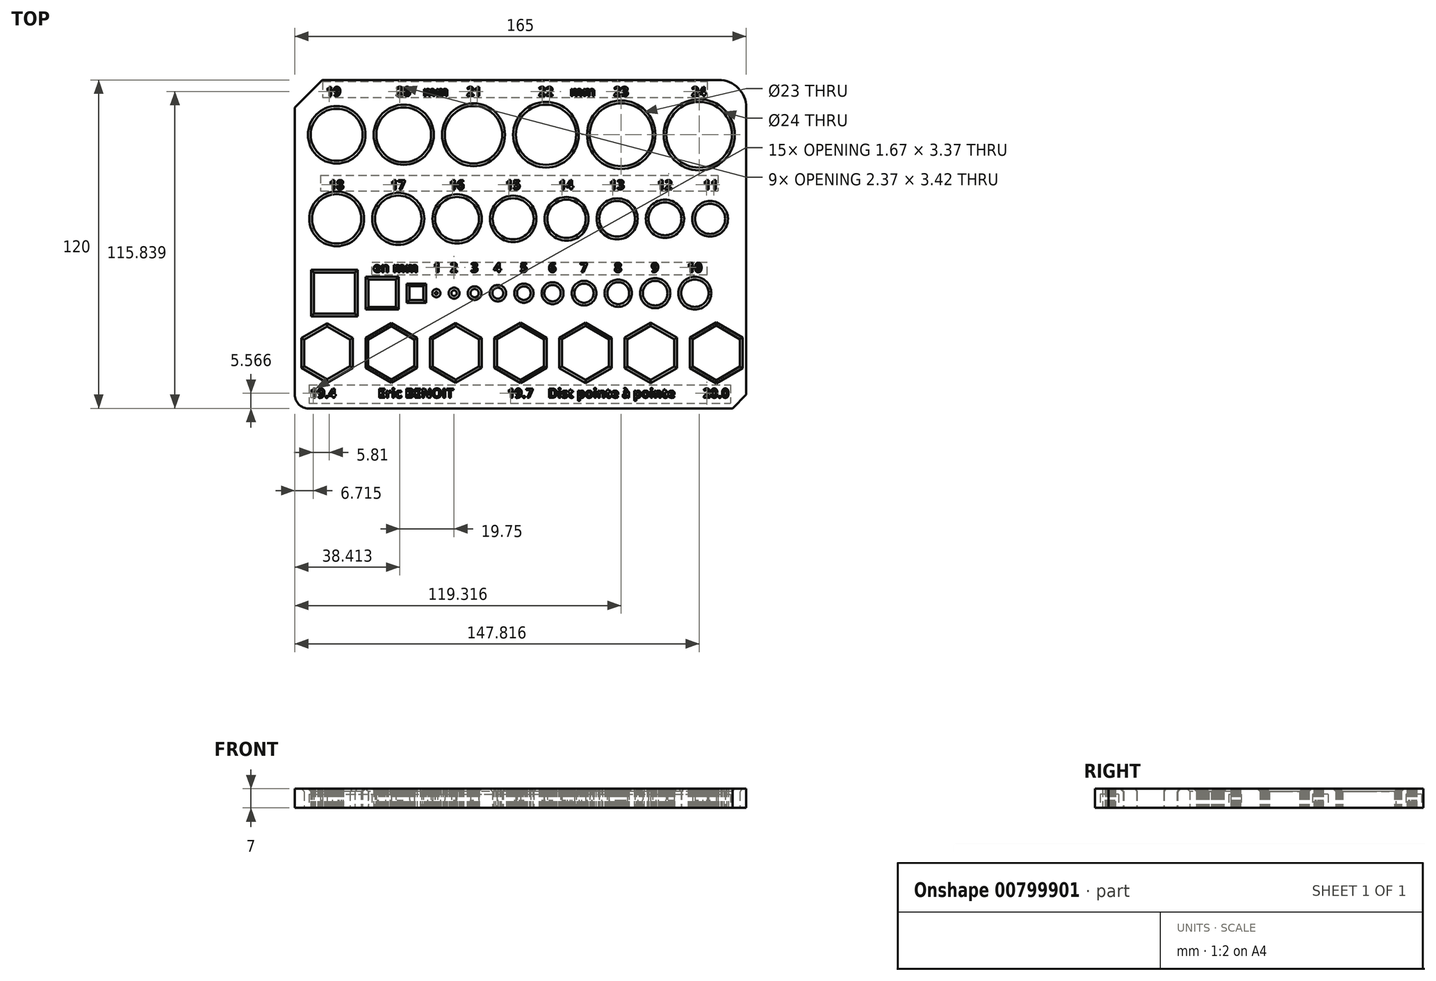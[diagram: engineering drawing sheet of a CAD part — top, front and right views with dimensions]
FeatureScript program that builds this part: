
annotation { "Feature Type Name" : "Feature", "Feature Type Description" : "" }
export const myFeature = defineFeature(function(context is Context, id is Id, definition is map)
    precondition{}
    {
        {
            var Q0;
            Q0=qCreatedBy(makeId("Top.planeOp"),FACE);
            var sketch = newSketch(context, id + "F0", { "sketchPlane" : qUnion([Q0])});
            skLineSegment(sketch, "E0.bottom", {"start": v(-82.5, 60) * mm, "end": v(82.5, 60) * mm});
            skLineSegment(sketch, "E0.top", {"start": v(-82.5, -60) * mm, "end": v(82.5, -60) * mm});
            skLineSegment(sketch, "E0.left", {"start": v(-82.5, 60) * mm, "end": v(-82.5, -60) * mm});
            skLineSegment(sketch, "E0.right", {"start": v(82.5, 60) * mm, "end": v(82.5, -60) * mm});
            skPoint(sketch, "E0.middle", {"position": v(0, 0) * mm});
            skLineSegment(sketch, "E1", {"start": v(-109.64, 40) * mm, "end": v(128.27, 40) * mm, "construction": true});
            skCircle(sketch, "E2", {"center": v(-67.18, 40) * mm, "radius": 9.5 * mm});
            skLineSegment(sketch, "E3.bottom", {"start": v(-57.68, 40) * mm, "end": v(-52.68, 40) * mm, "construction": true});
            skLineSegment(sketch, "E3.top", {"start": v(-57.68, 27.28) * mm, "end": v(-52.68, 27.28) * mm, "construction": true});
            skLineSegment(sketch, "E3.left", {"start": v(-57.68, 40) * mm, "end": v(-57.68, 27.28) * mm, "construction": true});
            skLineSegment(sketch, "E3.right", {"start": v(-52.68, 40) * mm, "end": v(-52.68, 27.28) * mm, "construction": true});
            skCircle(sketch, "E4", {"center": v(-42.68, 40) * mm, "radius": 10 * mm});
            skLineSegment(sketch, "E5.bottom", {"start": v(-32.68, 40) * mm, "end": v(-27.68, 40) * mm, "construction": true});
            skLineSegment(sketch, "E5.top", {"start": v(-32.68, 27.23) * mm, "end": v(-27.68, 27.23) * mm, "construction": true});
            skLineSegment(sketch, "E5.left", {"start": v(-32.68, 40) * mm, "end": v(-32.68, 27.23) * mm, "construction": true});
            skLineSegment(sketch, "E5.right", {"start": v(-27.68, 40) * mm, "end": v(-27.68, 27.23) * mm, "construction": true});
            skCircle(sketch, "E6", {"center": v(-17.18, 40) * mm, "radius": 10.5 * mm});
            skLineSegment(sketch, "E7.bottom", {"start": v(-6.68, 40) * mm, "end": v(-1.68, 40) * mm});
            skLineSegment(sketch, "E7.top", {"start": v(-6.68, 26.79) * mm, "end": v(-1.68, 26.79) * mm, "construction": true});
            skLineSegment(sketch, "E7.left", {"start": v(-6.68, 40) * mm, "end": v(-6.68, 26.79) * mm, "construction": true});
            skLineSegment(sketch, "E7.right", {"start": v(-1.68, 40) * mm, "end": v(-1.68, 26.79) * mm, "construction": true});
            skCircle(sketch, "E8", {"center": v(9.32, 40) * mm, "radius": 11 * mm});
            skLineSegment(sketch, "E9.bottom", {"start": v(20.32, 40) * mm, "end": v(25.32, 40) * mm});
            skLineSegment(sketch, "E9.top", {"start": v(20.32, 26.79) * mm, "end": v(25.32, 26.79) * mm, "construction": true});
            skLineSegment(sketch, "E9.left", {"start": v(20.32, 40) * mm, "end": v(20.32, 26.79) * mm, "construction": true});
            skLineSegment(sketch, "E9.right", {"start": v(25.32, 40) * mm, "end": v(25.32, 26.79) * mm, "construction": true});
            skCircle(sketch, "E10", {"center": v(36.82, 40) * mm, "radius": 11.5 * mm});
            skLineSegment(sketch, "E11.bottom", {"start": v(48.32, 40) * mm, "end": v(53.32, 40) * mm});
            skLineSegment(sketch, "E11.top", {"start": v(48.32, 25.73) * mm, "end": v(53.32, 25.73) * mm, "construction": true});
            skLineSegment(sketch, "E11.left", {"start": v(48.32, 40) * mm, "end": v(48.32, 25.73) * mm, "construction": true});
            skLineSegment(sketch, "E11.right", {"start": v(53.32, 40) * mm, "end": v(53.32, 25.73) * mm, "construction": true});
            skCircle(sketch, "E12", {"center": v(65.32, 40) * mm, "radius": 12 * mm});
            skLineSegment(sketch, "E13", {"start": v(-86.72, 9.27) * mm, "end": v(82.69, 9.27) * mm, "construction": true});
            skCircle(sketch, "E14", {"center": v(-67.18, 9.27) * mm, "radius": 9 * mm});
            skLineSegment(sketch, "E15.bottom", {"start": v(-58.18, 9.27) * mm, "end": v(-53.18, 9.27) * mm, "construction": true});
            skLineSegment(sketch, "E15.top", {"start": v(-58.18, -2.69) * mm, "end": v(-53.18, -2.69) * mm, "construction": true});
            skLineSegment(sketch, "E15.left", {"start": v(-58.18, 9.27) * mm, "end": v(-58.18, -2.69) * mm, "construction": true});
            skLineSegment(sketch, "E15.right", {"start": v(-53.18, 9.27) * mm, "end": v(-53.18, -2.69) * mm, "construction": true});
            skCircle(sketch, "E16", {"center": v(-44.68, 9.27) * mm, "radius": 8.5 * mm});
            skLineSegment(sketch, "E17.bottom", {"start": v(-36.18, 9.27) * mm, "end": v(-31.18, 9.27) * mm, "construction": true});
            skLineSegment(sketch, "E17.top", {"start": v(-36.18, -2.69) * mm, "end": v(-31.18, -2.69) * mm, "construction": true});
            skLineSegment(sketch, "E17.left", {"start": v(-36.18, 9.27) * mm, "end": v(-36.18, -2.69) * mm, "construction": true});
            skLineSegment(sketch, "E17.right", {"start": v(-31.18, 9.27) * mm, "end": v(-31.18, -2.69) * mm, "construction": true});
            skCircle(sketch, "E18", {"center": v(-23.18, 9.27) * mm, "radius": 8 * mm});
            skLineSegment(sketch, "E19.bottom", {"start": v(-15.18, 9.27) * mm, "end": v(-10.18, 9.27) * mm, "construction": true});
            skLineSegment(sketch, "E19.top", {"start": v(-15.18, -3.01) * mm, "end": v(-10.18, -3.01) * mm, "construction": true});
            skLineSegment(sketch, "E19.left", {"start": v(-15.18, 9.27) * mm, "end": v(-15.18, -3.01) * mm, "construction": true});
            skLineSegment(sketch, "E19.right", {"start": v(-10.18, 9.27) * mm, "end": v(-10.18, -3.01) * mm, "construction": true});
            skCircle(sketch, "E20", {"center": v(-2.68, 9.27) * mm, "radius": 7.5 * mm});
            skLineSegment(sketch, "E21.bottom", {"start": v(4.82, 9.27) * mm, "end": v(9.82, 9.27) * mm, "construction": true});
            skLineSegment(sketch, "E21.top", {"start": v(4.82, -2.69) * mm, "end": v(9.82, -2.69) * mm, "construction": true});
            skLineSegment(sketch, "E21.left", {"start": v(4.82, 9.27) * mm, "end": v(4.82, -2.69) * mm, "construction": true});
            skLineSegment(sketch, "E21.right", {"start": v(9.82, 9.27) * mm, "end": v(9.82, -2.69) * mm, "construction": true});
            skCircle(sketch, "E22", {"center": v(16.82, 9.27) * mm, "radius": 7 * mm});
            skLineSegment(sketch, "E23.bottom", {"start": v(23.82, 9.27) * mm, "end": v(28.82, 9.27) * mm, "construction": true});
            skLineSegment(sketch, "E23.top", {"start": v(23.82, -2.69) * mm, "end": v(28.82, -2.69) * mm, "construction": true});
            skLineSegment(sketch, "E23.left", {"start": v(23.82, 9.27) * mm, "end": v(23.82, -2.69) * mm, "construction": true});
            skLineSegment(sketch, "E23.right", {"start": v(28.82, 9.27) * mm, "end": v(28.82, -2.69) * mm, "construction": true});
            skCircle(sketch, "E24", {"center": v(35.32, 9.27) * mm, "radius": 6.5 * mm});
            skLineSegment(sketch, "E25.bottom", {"start": v(41.82, 9.27) * mm, "end": v(46.82, 9.27) * mm, "construction": true});
            skLineSegment(sketch, "E25.top", {"start": v(41.82, -2.69) * mm, "end": v(46.82, -2.69) * mm, "construction": true});
            skLineSegment(sketch, "E25.left", {"start": v(41.82, 9.27) * mm, "end": v(41.82, -2.69) * mm, "construction": true});
            skLineSegment(sketch, "E25.right", {"start": v(46.82, 9.27) * mm, "end": v(46.82, -2.69) * mm, "construction": true});
            skCircle(sketch, "E26", {"center": v(52.82, 9.27) * mm, "radius": 6 * mm});
            skLineSegment(sketch, "E27.bottom", {"start": v(58.82, 9.27) * mm, "end": v(63.82, 9.27) * mm, "construction": true});
            skLineSegment(sketch, "E27.top", {"start": v(58.82, -2.69) * mm, "end": v(63.82, -2.69) * mm, "construction": true});
            skLineSegment(sketch, "E27.left", {"start": v(58.82, 9.27) * mm, "end": v(58.82, -2.69) * mm, "construction": true});
            skLineSegment(sketch, "E27.right", {"start": v(63.82, 9.27) * mm, "end": v(63.82, -2.69) * mm, "construction": true});
            skCircle(sketch, "E28", {"center": v(69.32, 9.27) * mm, "radius": 5.5 * mm});
            skLineSegment(sketch, "E29", {"start": v(-83.6, 57.53) * mm, "end": v(84.67, 57.53) * mm, "construction": true});
            skLineSegment(sketch, "E30", {"start": v(-83.6, 54.13) * mm, "end": v(84.67, 54.13) * mm, "construction": true});
            skText(sketch, "E31", { "text": "19", "fontName": "OpenSans-Bold.ttf"});
            skText(sketch, "E32", { "text": "20", "fontName": "OpenSans-Bold.ttf"});
            skText(sketch, "E33", { "text": "21", "fontName": "OpenSans-Bold.ttf"});
            skText(sketch, "E34", { "text": "22", "fontName": "OpenSans-Bold.ttf"});
            skText(sketch, "E35", { "text": "23", "fontName": "OpenSans-Bold.ttf"});
            skText(sketch, "E36", { "text": "24", "fontName": "OpenSans-Bold.ttf"});
            skLineSegment(sketch, "E37", {"start": v(-86.72, 23.43) * mm, "end": v(82.69, 23.43) * mm, "construction": true});
            skLineSegment(sketch, "E38", {"start": v(-86.72, 20.03) * mm, "end": v(82.69, 20.03) * mm, "construction": true});
            skText(sketch, "E39", { "text": "18", "fontName": "OpenSans-Bold.ttf"});
            skText(sketch, "E40", { "text": "17", "fontName": "OpenSans-Bold.ttf"});
            skText(sketch, "E41", { "text": "16", "fontName": "OpenSans-Bold.ttf"});
            skText(sketch, "E42", { "text": "15", "fontName": "OpenSans-Bold.ttf"});
            skText(sketch, "E43", { "text": "14", "fontName": "OpenSans-Bold.ttf"});
            skText(sketch, "E44", { "text": "13", "fontName": "OpenSans-Bold.ttf"});
            skText(sketch, "E45", { "text": "12", "fontName": "OpenSans-Bold.ttf"});
            skText(sketch, "E46", { "text": "11", "fontName": "OpenSans-Bold.ttf"});
            skLineSegment(sketch, "E47", {"start": v(-86.72, -6.8) * mm, "end": v(82.69, -6.8) * mm, "construction": true});
            skLineSegment(sketch, "E48", {"start": v(-86.72, -10.2) * mm, "end": v(82.69, -10.2) * mm, "construction": true});
            skLineSegment(sketch, "E49", {"start": v(-86.72, -17.89) * mm, "end": v(82.69, -17.89) * mm, "construction": true});
            skCircle(sketch, "E50", {"center": v(1.23, -17.89) * mm, "radius": 2.5 * mm});
            skLineSegment(sketch, "E51.bottom", {"start": v(3.73, -17.89) * mm, "end": v(8.73, -17.89) * mm, "construction": true});
            skLineSegment(sketch, "E51.top", {"start": v(3.73, -29.79) * mm, "end": v(8.73, -29.79) * mm, "construction": true});
            skLineSegment(sketch, "E51.left", {"start": v(3.73, -17.89) * mm, "end": v(3.73, -29.79) * mm, "construction": true});
            skLineSegment(sketch, "E51.right", {"start": v(8.73, -17.89) * mm, "end": v(8.73, -29.79) * mm, "construction": true});
            skCircle(sketch, "E52", {"center": v(11.73, -17.89) * mm, "radius": 3 * mm});
            skLineSegment(sketch, "E53.bottom", {"start": v(14.73, -17.89) * mm, "end": v(19.73, -17.89) * mm, "construction": true});
            skLineSegment(sketch, "E53.top", {"start": v(14.73, -29.79) * mm, "end": v(19.73, -29.79) * mm, "construction": true});
            skLineSegment(sketch, "E53.left", {"start": v(14.73, -17.89) * mm, "end": v(14.73, -29.79) * mm, "construction": true});
            skLineSegment(sketch, "E53.right", {"start": v(19.73, -17.89) * mm, "end": v(19.73, -29.79) * mm, "construction": true});
            skCircle(sketch, "E54", {"center": v(23.23, -17.89) * mm, "radius": 3.5 * mm});
            skLineSegment(sketch, "E55.bottom", {"start": v(26.73, -17.89) * mm, "end": v(31.73, -17.89) * mm, "construction": true});
            skLineSegment(sketch, "E55.top", {"start": v(26.73, -29.79) * mm, "end": v(31.73, -29.79) * mm, "construction": true});
            skLineSegment(sketch, "E55.left", {"start": v(26.73, -17.89) * mm, "end": v(26.73, -29.79) * mm, "construction": true});
            skLineSegment(sketch, "E55.right", {"start": v(31.73, -17.89) * mm, "end": v(31.73, -29.79) * mm, "construction": true});
            skCircle(sketch, "E56", {"center": v(35.73, -17.89) * mm, "radius": 4 * mm});
            skLineSegment(sketch, "E57.bottom", {"start": v(39.73, -17.89) * mm, "end": v(44.73, -17.89) * mm, "construction": true});
            skLineSegment(sketch, "E57.top", {"start": v(39.73, -29.79) * mm, "end": v(44.73, -29.79) * mm, "construction": true});
            skLineSegment(sketch, "E57.left", {"start": v(39.73, -17.89) * mm, "end": v(39.73, -29.79) * mm, "construction": true});
            skLineSegment(sketch, "E57.right", {"start": v(44.73, -17.89) * mm, "end": v(44.73, -29.79) * mm, "construction": true});
            skCircle(sketch, "E58", {"center": v(49.23, -17.89) * mm, "radius": 4.5 * mm});
            skLineSegment(sketch, "E59.bottom", {"start": v(53.73, -17.89) * mm, "end": v(58.73, -17.89) * mm, "construction": true});
            skLineSegment(sketch, "E59.top", {"start": v(53.73, -29.79) * mm, "end": v(58.73, -29.79) * mm, "construction": true});
            skLineSegment(sketch, "E59.left", {"start": v(53.73, -17.89) * mm, "end": v(53.73, -29.79) * mm, "construction": true});
            skLineSegment(sketch, "E59.right", {"start": v(58.73, -17.89) * mm, "end": v(58.73, -29.79) * mm, "construction": true});
            skCircle(sketch, "E60", {"center": v(63.73, -17.89) * mm, "radius": 5 * mm});
            skLineSegment(sketch, "E61.bottom", {"start": v(-1.27, -17.89) * mm, "end": v(-6.27, -17.89) * mm, "construction": true});
            skLineSegment(sketch, "E61.top", {"start": v(-1.27, -29.79) * mm, "end": v(-6.27, -29.79) * mm, "construction": true});
            skLineSegment(sketch, "E61.left", {"start": v(-1.27, -17.89) * mm, "end": v(-1.27, -29.79) * mm, "construction": true});
            skLineSegment(sketch, "E61.right", {"start": v(-6.27, -17.89) * mm, "end": v(-6.27, -29.79) * mm, "construction": true});
            skCircle(sketch, "E62", {"center": v(-8.27, -17.89) * mm, "radius": 2 * mm});
            skLineSegment(sketch, "E63.bottom", {"start": v(-10.27, -17.89) * mm, "end": v(-15.27, -17.89) * mm, "construction": true});
            skLineSegment(sketch, "E63.top", {"start": v(-10.27, -29.79) * mm, "end": v(-15.27, -29.79) * mm, "construction": true});
            skLineSegment(sketch, "E63.left", {"start": v(-10.27, -17.89) * mm, "end": v(-10.27, -29.79) * mm, "construction": true});
            skLineSegment(sketch, "E63.right", {"start": v(-15.27, -17.89) * mm, "end": v(-15.27, -29.79) * mm, "construction": true});
            skCircle(sketch, "E64", {"center": v(-16.77, -17.89) * mm, "radius": 1.5 * mm});
            skLineSegment(sketch, "E65.bottom", {"start": v(-18.27, -17.89) * mm, "end": v(-23.27, -17.89) * mm, "construction": true});
            skLineSegment(sketch, "E65.top", {"start": v(-18.27, -29.79) * mm, "end": v(-23.27, -29.79) * mm, "construction": true});
            skLineSegment(sketch, "E65.left", {"start": v(-18.27, -17.89) * mm, "end": v(-18.27, -29.79) * mm, "construction": true});
            skLineSegment(sketch, "E65.right", {"start": v(-23.27, -17.89) * mm, "end": v(-23.27, -29.79) * mm, "construction": true});
            skCircle(sketch, "E66", {"center": v(-24.27, -17.89) * mm, "radius": 1 * mm});
            skLineSegment(sketch, "E67.bottom", {"start": v(-25.27, -17.89) * mm, "end": v(-30.27, -17.89) * mm, "construction": true});
            skLineSegment(sketch, "E67.top", {"start": v(-25.27, -29.79) * mm, "end": v(-30.27, -29.79) * mm, "construction": true});
            skLineSegment(sketch, "E67.left", {"start": v(-25.27, -17.89) * mm, "end": v(-25.27, -29.79) * mm, "construction": true});
            skLineSegment(sketch, "E67.right", {"start": v(-30.27, -17.89) * mm, "end": v(-30.27, -29.79) * mm, "construction": true});
            skCircle(sketch, "E68", {"center": v(-30.77, -17.89) * mm, "radius": 0.5 * mm});
            skText(sketch, "E69", { "text": "10", "fontName": "OpenSans-Bold.ttf"});
            skText(sketch, "E70", { "text": "9", "fontName": "OpenSans-Bold.ttf"});
            skText(sketch, "E71", { "text": "8", "fontName": "OpenSans-Bold.ttf"});
            skText(sketch, "E72", { "text": "7", "fontName": "OpenSans-Bold.ttf"});
            skText(sketch, "E73", { "text": "6", "fontName": "OpenSans-Bold.ttf"});
            skText(sketch, "E74", { "text": "5", "fontName": "OpenSans-Bold.ttf"});
            skText(sketch, "E75", { "text": "4", "fontName": "OpenSans-Bold.ttf"});
            skText(sketch, "E76", { "text": "3", "fontName": "OpenSans-Bold.ttf"});
            skText(sketch, "E77", { "text": "2", "fontName": "OpenSans-Bold.ttf"});
            skText(sketch, "E78", { "text": "1", "fontName": "OpenSans-Bold.ttf"});
            skText(sketch, "E79", { "text": "mm", "fontName": "OpenSans-Bold.ttf"});
            skText(sketch, "E80", { "text": "mm", "fontName": "OpenSans-Bold.ttf"});
            skLineSegment(sketch, "E81.bottom", {"start": v(-75.55, -10.39) * mm, "end": v(-60.55, -10.39) * mm});
            skLineSegment(sketch, "E81.top", {"start": v(-75.55, -25.39) * mm, "end": v(-60.55, -25.39) * mm});
            skLineSegment(sketch, "E81.left", {"start": v(-75.55, -10.39) * mm, "end": v(-75.55, -25.39) * mm});
            skLineSegment(sketch, "E81.right", {"start": v(-60.55, -10.39) * mm, "end": v(-60.55, -25.39) * mm});
            skPoint(sketch, "E81.middle", {"position": v(-68.05, -17.89) * mm});
            skLineSegment(sketch, "E82.bottom", {"start": v(-60.55, -25.39) * mm, "end": v(-55.55, -25.39) * mm, "construction": true});
            skLineSegment(sketch, "E82.top", {"start": v(-60.55, -29.79) * mm, "end": v(-55.55, -29.79) * mm, "construction": true});
            skLineSegment(sketch, "E82.left", {"start": v(-60.55, -25.39) * mm, "end": v(-60.55, -29.79) * mm, "construction": true});
            skLineSegment(sketch, "E82.right", {"start": v(-55.55, -25.39) * mm, "end": v(-55.55, -29.79) * mm, "construction": true});
            skLineSegment(sketch, "E83.bottom", {"start": v(-55.55, -12.89) * mm, "end": v(-45.55, -12.89) * mm});
            skLineSegment(sketch, "E83.top", {"start": v(-55.55, -22.89) * mm, "end": v(-45.55, -22.89) * mm});
            skLineSegment(sketch, "E83.left", {"start": v(-55.55, -12.89) * mm, "end": v(-55.55, -22.89) * mm});
            skLineSegment(sketch, "E83.right", {"start": v(-45.55, -12.89) * mm, "end": v(-45.55, -22.89) * mm});
            skPoint(sketch, "E83.middle", {"position": v(-50.55, -17.89) * mm});
            skLineSegment(sketch, "E84.bottom", {"start": v(-45.55, -22.89) * mm, "end": v(-40.55, -22.89) * mm, "construction": true});
            skLineSegment(sketch, "E84.top", {"start": v(-45.55, -29.79) * mm, "end": v(-40.55, -29.79) * mm, "construction": true});
            skLineSegment(sketch, "E84.left", {"start": v(-45.55, -22.89) * mm, "end": v(-45.55, -29.79) * mm, "construction": true});
            skLineSegment(sketch, "E84.right", {"start": v(-40.55, -22.89) * mm, "end": v(-40.55, -29.79) * mm, "construction": true});
            skPoint(sketch, "E85.middle", {"position": v(-43.62, -17.89) * mm});
            skLineSegment(sketch, "E86.bottom", {"start": v(-40.55, -20.39) * mm, "end": v(-35.55, -20.39) * mm});
            skLineSegment(sketch, "E86.top", {"start": v(-40.55, -15.39) * mm, "end": v(-35.55, -15.39) * mm});
            skLineSegment(sketch, "E86.left", {"start": v(-40.55, -20.39) * mm, "end": v(-40.55, -15.39) * mm});
            skLineSegment(sketch, "E86.right", {"start": v(-35.55, -20.39) * mm, "end": v(-35.55, -15.39) * mm});
            skPoint(sketch, "E86.middle", {"position": v(-38.05, -17.89) * mm});
            skText(sketch, "E87", { "text": "en mm", "fontName": "OpenSans-Bold.ttf"});
            skLineSegment(sketch, "E88", {"start": v(-86.72, -39.72) * mm, "end": v(89.88, -39.72) * mm, "construction": true});
            skCircle(sketch, "E89", {"center": v(-70.65, -39.72) * mm, "radius": 9.7 * mm});
            skLineSegment(sketch, "E90.bottom", {"start": v(-60.95, -39.72) * mm, "end": v(-56.95, -39.72) * mm, "construction": true});
            skLineSegment(sketch, "E90.top", {"start": v(-60.95, -50.07) * mm, "end": v(-56.95, -50.07) * mm, "construction": true});
            skLineSegment(sketch, "E90.left", {"start": v(-60.95, -39.72) * mm, "end": v(-60.95, -50.07) * mm, "construction": true});
            skLineSegment(sketch, "E90.right", {"start": v(-56.95, -39.72) * mm, "end": v(-56.95, -50.07) * mm, "construction": true});
            skCircle(sketch, "E91", {"center": v(-47.2, -39.72) * mm, "radius": 9.75 * mm});
            skLineSegment(sketch, "E92.bottom", {"start": v(-37.45, -39.72) * mm, "end": v(-33.45, -39.72) * mm, "construction": true});
            skLineSegment(sketch, "E92.top", {"start": v(-37.45, -50.07) * mm, "end": v(-33.45, -50.07) * mm, "construction": true});
            skLineSegment(sketch, "E92.left", {"start": v(-37.45, -39.72) * mm, "end": v(-37.45, -50.07) * mm, "construction": true});
            skLineSegment(sketch, "E92.right", {"start": v(-33.45, -39.72) * mm, "end": v(-33.45, -50.07) * mm, "construction": true});
            skCircle(sketch, "E93", {"center": v(-23.65, -39.72) * mm, "radius": 9.8 * mm});
            skLineSegment(sketch, "E94.bottom", {"start": v(-13.85, -39.72) * mm, "end": v(-9.85, -39.72) * mm, "construction": true});
            skLineSegment(sketch, "E94.top", {"start": v(-13.85, -50.07) * mm, "end": v(-9.85, -50.07) * mm, "construction": true});
            skLineSegment(sketch, "E94.left", {"start": v(-13.85, -39.72) * mm, "end": v(-13.85, -50.07) * mm, "construction": true});
            skLineSegment(sketch, "E94.right", {"start": v(-9.85, -39.72) * mm, "end": v(-9.85, -50.07) * mm, "construction": true});
            skCircle(sketch, "E95", {"center": v(0, -39.72) * mm, "radius": 9.85 * mm});
            skLineSegment(sketch, "E96.bottom", {"start": v(9.85, -39.72) * mm, "end": v(13.85, -39.72) * mm, "construction": true});
            skLineSegment(sketch, "E96.top", {"start": v(9.85, -50.07) * mm, "end": v(13.85, -50.07) * mm, "construction": true});
            skLineSegment(sketch, "E96.left", {"start": v(9.85, -39.72) * mm, "end": v(9.85, -50.07) * mm, "construction": true});
            skLineSegment(sketch, "E96.right", {"start": v(13.85, -39.72) * mm, "end": v(13.85, -50.07) * mm, "construction": true});
            skCircle(sketch, "E97", {"center": v(23.75, -39.72) * mm, "radius": 9.9 * mm});
            skLineSegment(sketch, "E98.bottom", {"start": v(33.65, -39.72) * mm, "end": v(37.65, -39.72) * mm, "construction": true});
            skLineSegment(sketch, "E98.top", {"start": v(33.65, -50.07) * mm, "end": v(37.65, -50.07) * mm, "construction": true});
            skLineSegment(sketch, "E98.left", {"start": v(33.65, -39.72) * mm, "end": v(33.65, -50.07) * mm, "construction": true});
            skLineSegment(sketch, "E98.right", {"start": v(37.65, -39.72) * mm, "end": v(37.65, -50.07) * mm, "construction": true});
            skCircle(sketch, "E99", {"center": v(47.6, -39.72) * mm, "radius": 9.95 * mm});
            skLineSegment(sketch, "E100.bottom", {"start": v(57.55, -39.72) * mm, "end": v(61.55, -39.72) * mm, "construction": true});
            skLineSegment(sketch, "E100.top", {"start": v(57.55, -50.07) * mm, "end": v(61.55, -50.07) * mm, "construction": true});
            skLineSegment(sketch, "E100.left", {"start": v(57.55, -39.72) * mm, "end": v(57.55, -50.07) * mm, "construction": true});
            skLineSegment(sketch, "E100.right", {"start": v(61.55, -39.72) * mm, "end": v(61.55, -50.07) * mm, "construction": true});
            skCircle(sketch, "E101", {"center": v(71.55, -39.72) * mm, "radius": 10 * mm});
            skCircle(sketch, "E102.cCircle", {"center": v(-70.65, -39.72) * mm, "radius": 9.7 * mm, "construction": true});
            skLineSegment(sketch, "E102.0", {"start": v(-70.65, -30.02) * mm, "end": v(-62.25, -34.87) * mm});
            skLineSegment(sketch, "E102.1", {"start": v(-62.25, -34.87) * mm, "end": v(-62.25, -44.57) * mm});
            skLineSegment(sketch, "E102.2", {"start": v(-62.25, -44.57) * mm, "end": v(-70.65, -49.42) * mm});
            skLineSegment(sketch, "E102.3", {"start": v(-70.65, -49.42) * mm, "end": v(-79.05, -44.57) * mm});
            skLineSegment(sketch, "E102.4", {"start": v(-79.05, -44.57) * mm, "end": v(-79.05, -34.87) * mm});
            skLineSegment(sketch, "E102.5", {"start": v(-79.05, -34.87) * mm, "end": v(-70.65, -30.02) * mm});
            skCircle(sketch, "E103.cCircle", {"center": v(-47.2, -39.72) * mm, "radius": 9.75 * mm, "construction": true});
            skLineSegment(sketch, "E103.0", {"start": v(-47.2, -29.97) * mm, "end": v(-38.76, -34.84) * mm});
            skLineSegment(sketch, "E103.1", {"start": v(-38.76, -34.84) * mm, "end": v(-38.76, -44.6) * mm});
            skLineSegment(sketch, "E103.2", {"start": v(-38.76, -44.6) * mm, "end": v(-47.2, -49.47) * mm});
            skLineSegment(sketch, "E103.3", {"start": v(-47.2, -49.47) * mm, "end": v(-55.64, -44.6) * mm});
            skLineSegment(sketch, "E103.4", {"start": v(-55.64, -44.6) * mm, "end": v(-55.64, -34.84) * mm});
            skLineSegment(sketch, "E103.5", {"start": v(-55.64, -34.84) * mm, "end": v(-47.2, -29.97) * mm});
            skCircle(sketch, "E104.cCircle", {"center": v(-23.65, -39.72) * mm, "radius": 9.8 * mm, "construction": true});
            skLineSegment(sketch, "E104.0", {"start": v(-23.65, -29.92) * mm, "end": v(-15.16, -34.82) * mm});
            skLineSegment(sketch, "E104.1", {"start": v(-15.16, -34.82) * mm, "end": v(-15.16, -44.62) * mm});
            skLineSegment(sketch, "E104.2", {"start": v(-15.16, -44.62) * mm, "end": v(-23.65, -49.52) * mm});
            skLineSegment(sketch, "E104.3", {"start": v(-23.65, -49.52) * mm, "end": v(-32.14, -44.62) * mm});
            skLineSegment(sketch, "E104.4", {"start": v(-32.14, -44.62) * mm, "end": v(-32.14, -34.82) * mm});
            skLineSegment(sketch, "E104.5", {"start": v(-32.14, -34.82) * mm, "end": v(-23.65, -29.92) * mm});
            skCircle(sketch, "E105.cCircle", {"center": v(0, -39.72) * mm, "radius": 9.85 * mm, "construction": true});
            skLineSegment(sketch, "E105.0", {"start": v(0, -29.87) * mm, "end": v(8.53, -34.8) * mm});
            skLineSegment(sketch, "E105.1", {"start": v(8.53, -34.8) * mm, "end": v(8.53, -44.64) * mm});
            skLineSegment(sketch, "E105.2", {"start": v(8.53, -44.64) * mm, "end": v(0, -49.57) * mm});
            skLineSegment(sketch, "E105.3", {"start": v(0, -49.57) * mm, "end": v(-8.53, -44.64) * mm});
            skLineSegment(sketch, "E105.4", {"start": v(-8.53, -44.64) * mm, "end": v(-8.53, -34.8) * mm});
            skLineSegment(sketch, "E105.5", {"start": v(-8.53, -34.8) * mm, "end": v(0, -29.87) * mm});
            skCircle(sketch, "E106.cCircle", {"center": v(23.75, -39.72) * mm, "radius": 9.9 * mm, "construction": true});
            skLineSegment(sketch, "E106.0", {"start": v(23.75, -29.82) * mm, "end": v(32.32, -34.77) * mm});
            skLineSegment(sketch, "E106.1", {"start": v(32.32, -34.77) * mm, "end": v(32.32, -44.67) * mm});
            skLineSegment(sketch, "E106.2", {"start": v(32.32, -44.67) * mm, "end": v(23.75, -49.62) * mm});
            skLineSegment(sketch, "E106.3", {"start": v(23.75, -49.62) * mm, "end": v(15.18, -44.67) * mm});
            skLineSegment(sketch, "E106.4", {"start": v(15.18, -44.67) * mm, "end": v(15.18, -34.77) * mm});
            skLineSegment(sketch, "E106.5", {"start": v(15.18, -34.77) * mm, "end": v(23.75, -29.82) * mm});
            skCircle(sketch, "E107.cCircle", {"center": v(47.6, -39.72) * mm, "radius": 9.95 * mm, "construction": true});
            skLineSegment(sketch, "E107.0", {"start": v(47.6, -29.77) * mm, "end": v(56.22, -34.74) * mm});
            skLineSegment(sketch, "E107.1", {"start": v(56.22, -34.74) * mm, "end": v(56.22, -44.7) * mm});
            skLineSegment(sketch, "E107.2", {"start": v(56.22, -44.7) * mm, "end": v(47.6, -49.67) * mm});
            skLineSegment(sketch, "E107.3", {"start": v(47.6, -49.67) * mm, "end": v(38.98, -44.7) * mm});
            skLineSegment(sketch, "E107.4", {"start": v(38.98, -44.7) * mm, "end": v(38.98, -34.74) * mm});
            skLineSegment(sketch, "E107.5", {"start": v(38.98, -34.74) * mm, "end": v(47.6, -29.77) * mm});
            skCircle(sketch, "E108.cCircle", {"center": v(71.55, -39.72) * mm, "radius": 10 * mm, "construction": true});
            skLineSegment(sketch, "E108.0", {"start": v(71.55, -29.72) * mm, "end": v(80.21, -34.72) * mm});
            skLineSegment(sketch, "E108.1", {"start": v(80.21, -34.72) * mm, "end": v(80.21, -44.72) * mm});
            skLineSegment(sketch, "E108.2", {"start": v(80.21, -44.72) * mm, "end": v(71.55, -49.72) * mm});
            skLineSegment(sketch, "E108.3", {"start": v(71.55, -49.72) * mm, "end": v(62.89, -44.72) * mm});
            skLineSegment(sketch, "E108.4", {"start": v(62.89, -44.72) * mm, "end": v(62.89, -34.72) * mm});
            skLineSegment(sketch, "E108.5", {"start": v(62.89, -34.72) * mm, "end": v(71.55, -29.72) * mm});
            skLineSegment(sketch, "E109", {"start": v(-86.72, -52.72) * mm, "end": v(89.88, -52.72) * mm, "construction": true});
            skLineSegment(sketch, "E110", {"start": v(-86.72, -56.12) * mm, "end": v(89.88, -56.12) * mm, "construction": true});
            skText(sketch, "E111", { "text": "19.4", "fontName": "OpenSans-Bold.ttf"});
            skText(sketch, "E112", { "text": "19.7", "fontName": "OpenSans-Bold.ttf"});
            skText(sketch, "E113", { "text": "20.0", "fontName": "OpenSans-Bold.ttf"});
            skText(sketch, "E114", { "text": "Dist pointe à pointe", "fontName": "OpenSans-Bold.ttf"});
            skText(sketch, "E115", { "text": "Eric BENOIT", "fontName": "OpenSans-Bold.ttf"});
            skLineSegment(sketch, "E116.left", {"start": v(82.5, 19.06) * mm, "end": v(82.5, 25.1) * mm});
            const initialGuessF0  = {"E31": [-0.07109, 0.05413, 1, 0, 0.0034], "E32": [-0.04545, 0.05413, 1, 0, 0.0034], "E33": [-0.01966, 0.05413, 1, 0, 0.0034], "E34": [0.00654, 0.05413, 1, 0, 0.0034], "E35": [0.03406, 0.05413, 1, 0, 0.0034], "E36": [0.0625, 0.05413, 1, 0, 0.0034], "E39": [-0.06995, 0.02003, 1, 0, 0.0034], "E40": [-0.04746, 0.02003, 1, 0, 0.0034], "E41": [-0.02596, 0.02003, 1, 0, 0.0034], "E42": [-0.00543, 0.02003, 1, 0, 0.0034], "E43": [0.014, 0.02003, 1, 0, 0.0034], "E44": [0.03256, 0.02003, 1, 0, 0.0034], "E45": [0.05004, 0.02003, 1, 0, 0.0034], "E46": [0.06684, 0.02003, 1, 0, 0.0034], "E69": [0.06096, -0.0102, 1, 0, 0.0034], "E70": [0.0478, -0.0102, 1, 0, 0.0034], "E71": [0.0343, -0.0102, 1, 0, 0.0034], "E72": [0.0218, -0.0102, 1, 0, 0.0034], "E73": [0.0103, -0.0102, 1, 0, 0.0034], "E74": [-0.00017, -0.0102, 1, 0, 0.0034], "E75": [-0.00974, -0.0102, 1, 0, 0.0034], "E76": [-0.01818, -0.0102, 1, 0, 0.0034], "E77": [-0.0257, -0.0102, 1, 0, 0.0034], "E78": [-0.0319, -0.0102, 1, 0, 0.0034], "E79": [-0.03562, 0.05413, 1, 0, 0.0034], "E80": [0.01807, 0.05413, 1, 0, 0.0034], "E87": [-0.05384, -0.0102, 1, 0, 0.0034], "E111": [-0.0769, -0.05612, 1, 0, 0.0034], "E112": [-0.0048, -0.05612, 1, 0, 0.0034], "E113": [0.06676, -0.05612, 1, 0, 0.0034], "E114": [0.01008, -0.05612, 1, 0, 0.0034], "E115": [-0.052, -0.05612, 1, 0, 0.0034]};
            skSetInitialGuess(sketch, initialGuessF0);
            skSolve(sketch);
        }
        {
            var Q0;
            Q0=makeQuery(id+"F0.imprint","IMPRINT",FACE,{"disambiguationData":[TD([[makeQuery(id+"F0.imprint","IMPRINT",EDGE,{"derivedFrom":sQuery(id+"F0.wireOp",EDGE,"E114.sketch_text.stroke-88")}),1.0]])]});
            var Q1;
            Q1=makeQuery(id+"F0.imprint","IMPRINT",FACE,{"disambiguationData":[TD([[makeQuery(id+"F0.imprint","IMPRINT",EDGE,{"derivedFrom":sQuery(id+"F0.wireOp",EDGE,"E0.bottom")}),-1.0]])]});
            var Q2;
            Q2=makeQuery(id+"F0.imprint","IMPRINT",FACE,{"disambiguationData":[TD([[makeQuery(id+"F0.imprint","IMPRINT",EDGE,{"derivedFrom":sQuery(id+"F0.wireOp",EDGE,"E73.sketch_text.stroke-25")}),1.0]])]});
            var Q3;
            Q3=makeQuery(id+"F0.imprint","IMPRINT",FACE,{"disambiguationData":[TD([[makeQuery(id+"F0.imprint","IMPRINT",EDGE,{"derivedFrom":sQuery(id+"F0.wireOp",EDGE,"E71.sketch_text.stroke-24")}),1.0]])]});
            var Q4;
            Q4=makeQuery(id+"F0.imprint","IMPRINT",FACE,{"disambiguationData":[TD([[makeQuery(id+"F0.imprint","IMPRINT",EDGE,{"derivedFrom":sQuery(id+"F0.wireOp",EDGE,"E71.sketch_text.stroke-31")}),1.0]])]});
            var Q5;
            Q5=makeQuery(id+"F0.imprint","IMPRINT",FACE,{"disambiguationData":[TD([[makeQuery(id+"F0.imprint","IMPRINT",EDGE,{"derivedFrom":sQuery(id+"F0.wireOp",EDGE,"E70.sketch_text.stroke-26")}),1.0]])]});
            var Q6;
            Q6=makeQuery(id+"F0.imprint","IMPRINT",FACE,{"disambiguationData":[TD([[makeQuery(id+"F0.imprint","IMPRINT",EDGE,{"derivedFrom":sQuery(id+"F0.wireOp",EDGE,"E69.sketch_text.stroke-18")}),1.0]])]});
            var Q7;
            {var subQ0=sQuery(id+"F0.wireOp",EDGE,"E107.1");Q7=makeQuery(id+"F0.imprint","IMPRINT",FACE,{"disambiguationData":[TD([[makeQuery(id+"F0.imprint","IMPRINT",EDGE,{"derivedFrom":subQ0}),1.0]])]});}
            var Q8;
            {var subQ0=sQuery(id+"F0.wireOp",EDGE,"E107.0");Q8=makeQuery(id+"F0.imprint","IMPRINT",FACE,{"disambiguationData":[TD([[makeQuery(id+"F0.imprint","IMPRINT",EDGE,{"derivedFrom":subQ0}),1.0]])]});}
            var Q9;
            {var subQ0=sQuery(id+"F0.wireOp",EDGE,"E107.5");Q9=makeQuery(id+"F0.imprint","IMPRINT",FACE,{"disambiguationData":[TD([[makeQuery(id+"F0.imprint","IMPRINT",EDGE,{"derivedFrom":subQ0}),1.0]])]});}
            var Q10;
            {var subQ0=sQuery(id+"F0.wireOp",EDGE,"E107.4");Q10=makeQuery(id+"F0.imprint","IMPRINT",FACE,{"disambiguationData":[TD([[makeQuery(id+"F0.imprint","IMPRINT",EDGE,{"derivedFrom":subQ0}),1.0]])]});}
            var Q11;
            {var subQ0=sQuery(id+"F0.wireOp",EDGE,"E107.3");Q11=makeQuery(id+"F0.imprint","IMPRINT",FACE,{"disambiguationData":[TD([[makeQuery(id+"F0.imprint","IMPRINT",EDGE,{"derivedFrom":subQ0}),1.0]])]});}
            var Q12;
            {var subQ0=sQuery(id+"F0.wireOp",EDGE,"E107.2");Q12=makeQuery(id+"F0.imprint","IMPRINT",FACE,{"disambiguationData":[TD([[makeQuery(id+"F0.imprint","IMPRINT",EDGE,{"derivedFrom":subQ0}),1.0]])]});}
            var Q13;
            {var subQ0=sQuery(id+"F0.wireOp",EDGE,"E108.4");Q13=makeQuery(id+"F0.imprint","IMPRINT",FACE,{"disambiguationData":[TD([[makeQuery(id+"F0.imprint","IMPRINT",EDGE,{"derivedFrom":subQ0}),1.0]])]});}
            var Q14;
            {var subQ0=sQuery(id+"F0.wireOp",EDGE,"E108.5");Q14=makeQuery(id+"F0.imprint","IMPRINT",FACE,{"disambiguationData":[TD([[makeQuery(id+"F0.imprint","IMPRINT",EDGE,{"derivedFrom":subQ0}),1.0]])]});}
            var Q15;
            {var subQ0=sQuery(id+"F0.wireOp",EDGE,"E108.0");Q15=makeQuery(id+"F0.imprint","IMPRINT",FACE,{"disambiguationData":[TD([[makeQuery(id+"F0.imprint","IMPRINT",EDGE,{"derivedFrom":subQ0}),1.0]])]});}
            var Q16;
            {var subQ0=sQuery(id+"F0.wireOp",EDGE,"E108.1");Q16=makeQuery(id+"F0.imprint","IMPRINT",FACE,{"disambiguationData":[TD([[makeQuery(id+"F0.imprint","IMPRINT",EDGE,{"derivedFrom":subQ0}),1.0]])]});}
            var Q17;
            {var subQ0=sQuery(id+"F0.wireOp",EDGE,"E108.2");Q17=makeQuery(id+"F0.imprint","IMPRINT",FACE,{"disambiguationData":[TD([[makeQuery(id+"F0.imprint","IMPRINT",EDGE,{"derivedFrom":subQ0}),1.0]])]});}
            var Q18;
            {var subQ0=sQuery(id+"F0.wireOp",EDGE,"E108.3");Q18=makeQuery(id+"F0.imprint","IMPRINT",FACE,{"disambiguationData":[TD([[makeQuery(id+"F0.imprint","IMPRINT",EDGE,{"derivedFrom":subQ0}),1.0]])]});}
            var Q19;
            Q19=makeQuery(id+"F0.imprint","IMPRINT",FACE,{"disambiguationData":[TD([[makeQuery(id+"F0.imprint","IMPRINT",EDGE,{"derivedFrom":sQuery(id+"F0.wireOp",EDGE,"E75.sketch_text.stroke-19")}),1.0]])]});
            var Q20;
            {var subQ0=sQuery(id+"F0.wireOp",EDGE,"E106.5");Q20=makeQuery(id+"F0.imprint","IMPRINT",FACE,{"disambiguationData":[TD([[makeQuery(id+"F0.imprint","IMPRINT",EDGE,{"derivedFrom":subQ0}),1.0]])]});}
            var Q21;
            {var subQ0=sQuery(id+"F0.wireOp",EDGE,"E106.0");Q21=makeQuery(id+"F0.imprint","IMPRINT",FACE,{"disambiguationData":[TD([[makeQuery(id+"F0.imprint","IMPRINT",EDGE,{"derivedFrom":subQ0}),1.0]])]});}
            var Q22;
            {var subQ0=sQuery(id+"F0.wireOp",EDGE,"E106.1");Q22=makeQuery(id+"F0.imprint","IMPRINT",FACE,{"disambiguationData":[TD([[makeQuery(id+"F0.imprint","IMPRINT",EDGE,{"derivedFrom":subQ0}),1.0]])]});}
            var Q23;
            {var subQ0=sQuery(id+"F0.wireOp",EDGE,"E106.2");Q23=makeQuery(id+"F0.imprint","IMPRINT",FACE,{"disambiguationData":[TD([[makeQuery(id+"F0.imprint","IMPRINT",EDGE,{"derivedFrom":subQ0}),1.0]])]});}
            var Q24;
            {var subQ0=sQuery(id+"F0.wireOp",EDGE,"E106.3");Q24=makeQuery(id+"F0.imprint","IMPRINT",FACE,{"disambiguationData":[TD([[makeQuery(id+"F0.imprint","IMPRINT",EDGE,{"derivedFrom":subQ0}),1.0]])]});}
            var Q25;
            {var subQ0=sQuery(id+"F0.wireOp",EDGE,"E106.4");Q25=makeQuery(id+"F0.imprint","IMPRINT",FACE,{"disambiguationData":[TD([[makeQuery(id+"F0.imprint","IMPRINT",EDGE,{"derivedFrom":subQ0}),1.0]])]});}
            var Q26;
            {var subQ0=sQuery(id+"F0.wireOp",EDGE,"E105.1");Q26=makeQuery(id+"F0.imprint","IMPRINT",FACE,{"disambiguationData":[TD([[makeQuery(id+"F0.imprint","IMPRINT",EDGE,{"derivedFrom":subQ0}),1.0]])]});}
            var Q27;
            {var subQ0=sQuery(id+"F0.wireOp",EDGE,"E105.2");Q27=makeQuery(id+"F0.imprint","IMPRINT",FACE,{"disambiguationData":[TD([[makeQuery(id+"F0.imprint","IMPRINT",EDGE,{"derivedFrom":subQ0}),1.0]])]});}
            var Q28;
            {var subQ0=sQuery(id+"F0.wireOp",EDGE,"E105.3");Q28=makeQuery(id+"F0.imprint","IMPRINT",FACE,{"disambiguationData":[TD([[makeQuery(id+"F0.imprint","IMPRINT",EDGE,{"derivedFrom":subQ0}),1.0]])]});}
            var Q29;
            {var subQ0=sQuery(id+"F0.wireOp",EDGE,"E105.4");Q29=makeQuery(id+"F0.imprint","IMPRINT",FACE,{"disambiguationData":[TD([[makeQuery(id+"F0.imprint","IMPRINT",EDGE,{"derivedFrom":subQ0}),1.0]])]});}
            var Q30;
            {var subQ0=sQuery(id+"F0.wireOp",EDGE,"E105.5");Q30=makeQuery(id+"F0.imprint","IMPRINT",FACE,{"disambiguationData":[TD([[makeQuery(id+"F0.imprint","IMPRINT",EDGE,{"derivedFrom":subQ0}),1.0]])]});}
            var Q31;
            {var subQ0=sQuery(id+"F0.wireOp",EDGE,"E105.0");Q31=makeQuery(id+"F0.imprint","IMPRINT",FACE,{"disambiguationData":[TD([[makeQuery(id+"F0.imprint","IMPRINT",EDGE,{"derivedFrom":subQ0}),1.0]])]});}
            var Q32;
            {var subQ0=sQuery(id+"F0.wireOp",EDGE,"E104.0");Q32=makeQuery(id+"F0.imprint","IMPRINT",FACE,{"disambiguationData":[TD([[makeQuery(id+"F0.imprint","IMPRINT",EDGE,{"derivedFrom":subQ0}),1.0]])]});}
            var Q33;
            {var subQ0=sQuery(id+"F0.wireOp",EDGE,"E104.5");Q33=makeQuery(id+"F0.imprint","IMPRINT",FACE,{"disambiguationData":[TD([[makeQuery(id+"F0.imprint","IMPRINT",EDGE,{"derivedFrom":subQ0}),1.0]])]});}
            var Q34;
            {var subQ0=sQuery(id+"F0.wireOp",EDGE,"E104.4");Q34=makeQuery(id+"F0.imprint","IMPRINT",FACE,{"disambiguationData":[TD([[makeQuery(id+"F0.imprint","IMPRINT",EDGE,{"derivedFrom":subQ0}),1.0]])]});}
            var Q35;
            {var subQ0=sQuery(id+"F0.wireOp",EDGE,"E104.3");Q35=makeQuery(id+"F0.imprint","IMPRINT",FACE,{"disambiguationData":[TD([[makeQuery(id+"F0.imprint","IMPRINT",EDGE,{"derivedFrom":subQ0}),1.0]])]});}
            var Q36;
            {var subQ0=sQuery(id+"F0.wireOp",EDGE,"E104.2");Q36=makeQuery(id+"F0.imprint","IMPRINT",FACE,{"disambiguationData":[TD([[makeQuery(id+"F0.imprint","IMPRINT",EDGE,{"derivedFrom":subQ0}),1.0]])]});}
            var Q37;
            {var subQ0=sQuery(id+"F0.wireOp",EDGE,"E104.1");Q37=makeQuery(id+"F0.imprint","IMPRINT",FACE,{"disambiguationData":[TD([[makeQuery(id+"F0.imprint","IMPRINT",EDGE,{"derivedFrom":subQ0}),1.0]])]});}
            var Q38;
            {var subQ0=sQuery(id+"F0.wireOp",EDGE,"E103.1");Q38=makeQuery(id+"F0.imprint","IMPRINT",FACE,{"disambiguationData":[TD([[makeQuery(id+"F0.imprint","IMPRINT",EDGE,{"derivedFrom":subQ0}),1.0]])]});}
            var Q39;
            {var subQ0=sQuery(id+"F0.wireOp",EDGE,"E103.0");Q39=makeQuery(id+"F0.imprint","IMPRINT",FACE,{"disambiguationData":[TD([[makeQuery(id+"F0.imprint","IMPRINT",EDGE,{"derivedFrom":subQ0}),1.0]])]});}
            var Q40;
            {var subQ0=sQuery(id+"F0.wireOp",EDGE,"E103.5");Q40=makeQuery(id+"F0.imprint","IMPRINT",FACE,{"disambiguationData":[TD([[makeQuery(id+"F0.imprint","IMPRINT",EDGE,{"derivedFrom":subQ0}),1.0]])]});}
            var Q41;
            {var subQ0=sQuery(id+"F0.wireOp",EDGE,"E103.4");Q41=makeQuery(id+"F0.imprint","IMPRINT",FACE,{"disambiguationData":[TD([[makeQuery(id+"F0.imprint","IMPRINT",EDGE,{"derivedFrom":subQ0}),1.0]])]});}
            var Q42;
            {var subQ0=sQuery(id+"F0.wireOp",EDGE,"E103.3");Q42=makeQuery(id+"F0.imprint","IMPRINT",FACE,{"disambiguationData":[TD([[makeQuery(id+"F0.imprint","IMPRINT",EDGE,{"derivedFrom":subQ0}),1.0]])]});}
            var Q43;
            {var subQ0=sQuery(id+"F0.wireOp",EDGE,"E103.2");Q43=makeQuery(id+"F0.imprint","IMPRINT",FACE,{"disambiguationData":[TD([[makeQuery(id+"F0.imprint","IMPRINT",EDGE,{"derivedFrom":subQ0}),1.0]])]});}
            var Q44;
            Q44=makeQuery(id+"F0.imprint","IMPRINT",FACE,{"disambiguationData":[TD([[makeQuery(id+"F0.imprint","IMPRINT",EDGE,{"derivedFrom":sQuery(id+"F0.wireOp",EDGE,"E111.sketch_text.stroke-28")}),1.0]])]});
            var Q45;
            Q45=makeQuery(id+"F0.imprint","IMPRINT",FACE,{"disambiguationData":[TD([[makeQuery(id+"F0.imprint","IMPRINT",EDGE,{"derivedFrom":sQuery(id+"F0.wireOp",EDGE,"E111.sketch_text.stroke-55")}),1.0]])]});
            var Q46;
            Q46=makeQuery(id+"F0.imprint","IMPRINT",FACE,{"disambiguationData":[TD([[makeQuery(id+"F0.imprint","IMPRINT",EDGE,{"derivedFrom":sQuery(id+"F0.wireOp",EDGE,"E115.sketch_text.stroke-60")}),1.0]])]});
            var Q47;
            Q47=makeQuery(id+"F0.imprint","IMPRINT",FACE,{"disambiguationData":[TD([[makeQuery(id+"F0.imprint","IMPRINT",EDGE,{"derivedFrom":sQuery(id+"F0.wireOp",EDGE,"E112.sketch_text.stroke-28")}),1.0]])]});
            var Q48;
            Q48=makeQuery(id+"F0.imprint","IMPRINT",FACE,{"disambiguationData":[TD([[makeQuery(id+"F0.imprint","IMPRINT",EDGE,{"derivedFrom":sQuery(id+"F0.wireOp",EDGE,"E114.sketch_text.stroke-7")}),1.0]])]});
            var Q49;
            Q49=makeQuery(id+"F0.imprint","IMPRINT",FACE,{"disambiguationData":[TD([[makeQuery(id+"F0.imprint","IMPRINT",EDGE,{"derivedFrom":sQuery(id+"F0.wireOp",EDGE,"E114.sketch_text.stroke-80")}),1.0]])]});
            var Q50;
            Q50=makeQuery(id+"F0.imprint","IMPRINT",FACE,{"disambiguationData":[TD([[makeQuery(id+"F0.imprint","IMPRINT",EDGE,{"derivedFrom":sQuery(id+"F0.wireOp",EDGE,"E113.sketch_text.stroke-32")}),1.0]])]});
            var Q51;
            Q51=makeQuery(id+"F0.imprint","IMPRINT",FACE,{"disambiguationData":[TD([[makeQuery(id+"F0.imprint","IMPRINT",EDGE,{"derivedFrom":sQuery(id+"F0.wireOp",EDGE,"E113.sketch_text.stroke-56")}),1.0]])]});
            var Q52;
            Q52=makeQuery(id+"F0.imprint","IMPRINT",FACE,{"disambiguationData":[TD([[makeQuery(id+"F0.imprint","IMPRINT",EDGE,{"derivedFrom":sQuery(id+"F0.wireOp",EDGE,"E114.sketch_text.stroke-217")}),1.0]])]});
            var Q53;
            Q53=makeQuery(id+"F0.imprint","IMPRINT",FACE,{"disambiguationData":[TD([[makeQuery(id+"F0.imprint","IMPRINT",EDGE,{"derivedFrom":sQuery(id+"F0.wireOp",EDGE,"E114.sketch_text.stroke-225")}),1.0]])]});
            var Q54;
            Q54=makeQuery(id+"F0.imprint","IMPRINT",FACE,{"disambiguationData":[TD([[makeQuery(id+"F0.imprint","IMPRINT",EDGE,{"derivedFrom":sQuery(id+"F0.wireOp",EDGE,"E114.sketch_text.stroke-150")}),1.0]])]});
            var Q55;
            Q55=makeQuery(id+"F0.imprint","IMPRINT",FACE,{"disambiguationData":[TD([[makeQuery(id+"F0.imprint","IMPRINT",EDGE,{"derivedFrom":sQuery(id+"F0.wireOp",EDGE,"E114.sketch_text.stroke-188")}),1.0]])]});
            var Q56;
            Q56=makeQuery(id+"F0.imprint","IMPRINT",FACE,{"disambiguationData":[TD([[makeQuery(id+"F0.imprint","IMPRINT",EDGE,{"derivedFrom":sQuery(id+"F0.wireOp",EDGE,"E114.sketch_text.stroke-287")}),1.0]])]});
            var Q57;
            Q57=makeQuery(id+"F0.imprint","IMPRINT",FACE,{"disambiguationData":[TD([[makeQuery(id+"F0.imprint","IMPRINT",EDGE,{"derivedFrom":sQuery(id+"F0.wireOp",EDGE,"E41.sketch_text.stroke-27")}),1.0]])]});
            var Q58;
            Q58=makeQuery(id+"F0.imprint","IMPRINT",FACE,{"disambiguationData":[TD([[makeQuery(id+"F0.imprint","IMPRINT",EDGE,{"derivedFrom":sQuery(id+"F0.wireOp",EDGE,"E43.sketch_text.stroke-21")}),1.0]])]});
            var Q59;
            Q59=makeQuery(id+"F0.imprint","IMPRINT",FACE,{"disambiguationData":[TD([[makeQuery(id+"F0.imprint","IMPRINT",EDGE,{"derivedFrom":sQuery(id+"F0.wireOp",EDGE,"E31.sketch_text.stroke-28")}),1.0]])]});
            var Q60;
            Q60=makeQuery(id+"F0.imprint","IMPRINT",FACE,{"disambiguationData":[TD([[makeQuery(id+"F0.imprint","IMPRINT",EDGE,{"derivedFrom":sQuery(id+"F0.wireOp",EDGE,"E32.sketch_text.stroke-32")}),1.0]])]});
            var Q61;
            Q61=makeQuery(id+"F0.imprint","IMPRINT",FACE,{"disambiguationData":[TD([[makeQuery(id+"F0.imprint","IMPRINT",EDGE,{"derivedFrom":sQuery(id+"F0.wireOp",EDGE,"E36.sketch_text.stroke-35")}),1.0]])]});
            var Q62;
            Q62=makeQuery(id+"F0.imprint","IMPRINT",FACE,{"disambiguationData":[TD([[makeQuery(id+"F0.imprint","IMPRINT",EDGE,{"derivedFrom":sQuery(id+"F0.wireOp",EDGE,"E87.sketch_text.stroke-0")}),1.0]])]});
            var Q63;
            Q63=makeQuery(id+"F0.imprint","IMPRINT",FACE,{"disambiguationData":[TD([[makeQuery(id+"F0.imprint","IMPRINT",EDGE,{"derivedFrom":sQuery(id+"F0.wireOp",EDGE,"E115.sketch_text.stroke-107")}),1.0]])]});
            var Q64;
            Q64=makeQuery(id+"F0.imprint","IMPRINT",FACE,{"disambiguationData":[TD([[makeQuery(id+"F0.imprint","IMPRINT",EDGE,{"derivedFrom":sQuery(id+"F0.wireOp",EDGE,"E115.sketch_text.stroke-67")}),1.0]])]});
            var Q65;
            {var subQ0=sQuery(id+"F0.wireOp",EDGE,"E102.4");Q65=makeQuery(id+"F0.imprint","IMPRINT",FACE,{"disambiguationData":[TD([[makeQuery(id+"F0.imprint","IMPRINT",EDGE,{"derivedFrom":subQ0}),1.0]])]});}
            var Q66;
            {var subQ0=sQuery(id+"F0.wireOp",EDGE,"E102.5");Q66=makeQuery(id+"F0.imprint","IMPRINT",FACE,{"disambiguationData":[TD([[makeQuery(id+"F0.imprint","IMPRINT",EDGE,{"derivedFrom":subQ0}),1.0]])]});}
            var Q67;
            {var subQ0=sQuery(id+"F0.wireOp",EDGE,"E102.0");Q67=makeQuery(id+"F0.imprint","IMPRINT",FACE,{"disambiguationData":[TD([[makeQuery(id+"F0.imprint","IMPRINT",EDGE,{"derivedFrom":subQ0}),1.0]])]});}
            var Q68;
            {var subQ0=sQuery(id+"F0.wireOp",EDGE,"E102.1");Q68=makeQuery(id+"F0.imprint","IMPRINT",FACE,{"disambiguationData":[TD([[makeQuery(id+"F0.imprint","IMPRINT",EDGE,{"derivedFrom":subQ0}),1.0]])]});}
            var Q69;
            {var subQ0=sQuery(id+"F0.wireOp",EDGE,"E102.2");Q69=makeQuery(id+"F0.imprint","IMPRINT",FACE,{"disambiguationData":[TD([[makeQuery(id+"F0.imprint","IMPRINT",EDGE,{"derivedFrom":subQ0}),1.0]])]});}
            var Q70;
            {var subQ0=sQuery(id+"F0.wireOp",EDGE,"E102.3");Q70=makeQuery(id+"F0.imprint","IMPRINT",FACE,{"disambiguationData":[TD([[makeQuery(id+"F0.imprint","IMPRINT",EDGE,{"derivedFrom":subQ0}),1.0]])]});}
            var Q71;
            Q71=makeQuery(id+"F0.imprint","IMPRINT",FACE,{"disambiguationData":[TD([[makeQuery(id+"F0.imprint","IMPRINT",EDGE,{"derivedFrom":sQuery(id+"F0.wireOp",EDGE,"E39.sketch_text.stroke-26")}),1.0]])]});
            var Q72;
            Q72=makeQuery(id+"F0.imprint","IMPRINT",FACE,{"disambiguationData":[TD([[makeQuery(id+"F0.imprint","IMPRINT",EDGE,{"derivedFrom":sQuery(id+"F0.wireOp",EDGE,"E39.sketch_text.stroke-33")}),1.0]])]});
            var Q73;
            Q73=makeQuery(id+"F0.imprint","IMPRINT",FACE,{"disambiguationData":[TD([[makeQuery(id+"F0.imprint","IMPRINT",EDGE,{"derivedFrom":sQuery(id+"F0.wireOp",EDGE,"E75.sketch_text.stroke-11")}),1.0]])]});
            var Q74;
            Q74=makeQuery(id+"F0.imprint","IMPRINT",FACE,{"disambiguationData":[TD([[makeQuery(id+"F0.imprint","IMPRINT",EDGE,{"derivedFrom":sQuery(id+"F0.wireOp",EDGE,"E73.sketch_text.stroke-17")}),1.0]])]});
            var Q75;
            Q75=makeQuery(id+"F0.imprint","IMPRINT",FACE,{"disambiguationData":[TD([[makeQuery(id+"F0.imprint","IMPRINT",EDGE,{"derivedFrom":sQuery(id+"F0.wireOp",EDGE,"E71.sketch_text.stroke-16")}),1.0]])]});
            var Q76;
            Q76=makeQuery(id+"F0.imprint","IMPRINT",FACE,{"disambiguationData":[TD([[makeQuery(id+"F0.imprint","IMPRINT",EDGE,{"derivedFrom":sQuery(id+"F0.wireOp",EDGE,"E70.sketch_text.stroke-18")}),1.0]])]});
            var Q77;
            Q77=makeQuery(id+"F0.imprint","IMPRINT",FACE,{"disambiguationData":[TD([[makeQuery(id+"F0.imprint","IMPRINT",EDGE,{"derivedFrom":sQuery(id+"F0.wireOp",EDGE,"E69.sketch_text.stroke-0")}),1.0]])]});
            var Q78;
            Q78=makeQuery(id+"F0.imprint","IMPRINT",FACE,{"disambiguationData":[TD([[makeQuery(id+"F0.imprint","IMPRINT",EDGE,{"derivedFrom":sQuery(id+"F0.wireOp",EDGE,"E31.sketch_text.stroke-0")}),1.0]])]});
            var Q79;
            Q79=makeQuery(id+"F0.imprint","IMPRINT",FACE,{"disambiguationData":[TD([[makeQuery(id+"F0.imprint","IMPRINT",EDGE,{"derivedFrom":sQuery(id+"F0.wireOp",EDGE,"E39.sketch_text.stroke-0")}),1.0]])]});
            var Q80;
            Q80=makeQuery(id+"F0.imprint","IMPRINT",FACE,{"disambiguationData":[TD([[makeQuery(id+"F0.imprint","IMPRINT",EDGE,{"derivedFrom":sQuery(id+"F0.wireOp",EDGE,"E111.sketch_text.stroke-0")}),1.0]])]});
            extrude(context, id + "F1", {"entities" : qUnion([Q0, Q1, Q2, Q3, Q4, Q5, Q6, Q7, Q8, Q9, Q10, Q11, Q12, Q13, Q14, Q15, Q16, Q17, Q18, Q19, Q20, Q21, Q22, Q23, Q24, Q25, Q26, Q27, Q28, Q29, Q30, Q31, Q32, Q33, Q34, Q35, Q36, Q37, Q38, Q39, Q40, Q41, Q42, Q43, Q44, Q45, Q46, Q47, Q48, Q49, Q50, Q51, Q52, Q53, Q54, Q55, Q56, Q57, Q58, Q59, Q60, Q61, Q62, Q63, Q64, Q65, Q66, Q67, Q68, Q69, Q70, Q71, Q72, Q73, Q74, Q75, Q76, Q77, Q78, Q79, Q80]), "depth" : 7 * mm, "offsetDistance" : 25 * mm});
        }
        {
            var Q0;
            Q0=makeQuery(id+"F1.opExtrude","SWEPT_EDGE",EDGE,{"disambiguationData":[OSD([sQuery(id+"F0.wireOp",EDGE,"E0.bottom"),sQuery(id+"F0.wireOp",EDGE,"E0.right")])]});
            fillet(context, id + "F2", {"entities" : qUnion([Q0]), "radius" : 10 * mm, "tangentPropagation" : true, "allowEdgeOverflow" : false});
        }
        {
            var Q0;
            Q0=makeQuery(id+"F1.opExtrude","SWEPT_EDGE",EDGE,{"disambiguationData":[OSD([sQuery(id+"F0.wireOp",EDGE,"E0.top"),sQuery(id+"F0.wireOp",EDGE,"E0.right")])]});
            chamfer(context, id + "F3", {"entities" : qUnion([Q0]), "width" : 5 * mm, "tangentPropagation" : true});
        }
        {
            var Q0;
            Q0=makeQuery(id+"F1.opExtrude","SWEPT_EDGE",EDGE,{"disambiguationData":[OSD([sQuery(id+"F0.wireOp",EDGE,"E0.bottom"),sQuery(id+"F0.wireOp",EDGE,"E0.left")])]});
            chamfer(context, id + "F4", {"entities" : qUnion([Q0]), "width" : 10 * mm, "tangentPropagation" : true});
        }
        {
            var Q0;
            Q0=makeQuery(id+"F1.opExtrude","SWEPT_EDGE",EDGE,{"disambiguationData":[OSD([sQuery(id+"F0.wireOp",EDGE,"E0.top"),sQuery(id+"F0.wireOp",EDGE,"E0.left")])]});
            fillet(context, id + "F5", {"entities" : qUnion([Q0]), "radius" : 5 * mm, "tangentPropagation" : true, "allowEdgeOverflow" : false});
        }
        {
            var Q0;
            Q0=makeQuery(id+"F1.opExtrude","CAP_EDGE",EDGE,{"disambiguationData":[OSD([sQuery(id+"F0.wireOp",EDGE,"E102.5")])],"isStart":false});
            var Q1;
            Q1=makeQuery(id+"F1.opExtrude","CAP_EDGE",EDGE,{"disambiguationData":[OSD([sQuery(id+"F0.wireOp",EDGE,"E102.0")])],"isStart":false});
            var Q2;
            Q2=makeQuery(id+"F1.opExtrude","CAP_EDGE",EDGE,{"disambiguationData":[OSD([sQuery(id+"F0.wireOp",EDGE,"E102.1")])],"isStart":false});
            var Q3;
            Q3=makeQuery(id+"F1.opExtrude","CAP_EDGE",EDGE,{"disambiguationData":[OSD([sQuery(id+"F0.wireOp",EDGE,"E102.2")])],"isStart":false});
            var Q4;
            Q4=makeQuery(id+"F1.opExtrude","CAP_EDGE",EDGE,{"disambiguationData":[OSD([sQuery(id+"F0.wireOp",EDGE,"E102.3")])],"isStart":false});
            var Q5;
            Q5=makeQuery(id+"F1.opExtrude","CAP_EDGE",EDGE,{"disambiguationData":[OSD([sQuery(id+"F0.wireOp",EDGE,"E102.4")])],"isStart":false});
            var Q6;
            Q6=makeQuery(id+"F1.opExtrude","CAP_EDGE",EDGE,{"disambiguationData":[OSD([sQuery(id+"F0.wireOp",EDGE,"E103.4")])],"isStart":false});
            var Q7;
            Q7=makeQuery(id+"F1.opExtrude","CAP_EDGE",EDGE,{"disambiguationData":[OSD([sQuery(id+"F0.wireOp",EDGE,"E103.5")])],"isStart":false});
            var Q8;
            Q8=makeQuery(id+"F1.opExtrude","CAP_EDGE",EDGE,{"disambiguationData":[OSD([sQuery(id+"F0.wireOp",EDGE,"E103.0")])],"isStart":false});
            var Q9;
            Q9=makeQuery(id+"F1.opExtrude","CAP_EDGE",EDGE,{"disambiguationData":[OSD([sQuery(id+"F0.wireOp",EDGE,"E103.1")])],"isStart":false});
            var Q10;
            Q10=makeQuery(id+"F1.opExtrude","CAP_EDGE",EDGE,{"disambiguationData":[OSD([sQuery(id+"F0.wireOp",EDGE,"E103.2")])],"isStart":false});
            var Q11;
            Q11=makeQuery(id+"F1.opExtrude","CAP_EDGE",EDGE,{"disambiguationData":[OSD([sQuery(id+"F0.wireOp",EDGE,"E103.3")])],"isStart":false});
            var Q12;
            Q12=makeQuery(id+"F1.opExtrude","CAP_EDGE",EDGE,{"disambiguationData":[OSD([sQuery(id+"F0.wireOp",EDGE,"E104.4")])],"isStart":false});
            var Q13;
            Q13=makeQuery(id+"F1.opExtrude","CAP_EDGE",EDGE,{"disambiguationData":[OSD([sQuery(id+"F0.wireOp",EDGE,"E104.1")])],"isStart":false});
            var Q14;
            Q14=makeQuery(id+"F1.opExtrude","CAP_EDGE",EDGE,{"disambiguationData":[OSD([sQuery(id+"F0.wireOp",EDGE,"E105.4")])],"isStart":false});
            var Q15;
            Q15=makeQuery(id+"F1.opExtrude","CAP_EDGE",EDGE,{"disambiguationData":[OSD([sQuery(id+"F0.wireOp",EDGE,"E105.1")])],"isStart":false});
            var Q16;
            Q16=makeQuery(id+"F1.opExtrude","CAP_EDGE",EDGE,{"disambiguationData":[OSD([sQuery(id+"F0.wireOp",EDGE,"E105.3")])],"isStart":false});
            var Q17;
            Q17=makeQuery(id+"F1.opExtrude","CAP_EDGE",EDGE,{"disambiguationData":[OSD([sQuery(id+"F0.wireOp",EDGE,"E105.2")])],"isStart":false});
            var Q18;
            Q18=makeQuery(id+"F1.opExtrude","CAP_EDGE",EDGE,{"disambiguationData":[OSD([sQuery(id+"F0.wireOp",EDGE,"E105.0")])],"isStart":false});
            var Q19;
            Q19=makeQuery(id+"F1.opExtrude","CAP_EDGE",EDGE,{"disambiguationData":[OSD([sQuery(id+"F0.wireOp",EDGE,"E105.5")])],"isStart":false});
            var Q20;
            Q20=makeQuery(id+"F1.opExtrude","CAP_EDGE",EDGE,{"disambiguationData":[OSD([sQuery(id+"F0.wireOp",EDGE,"E104.0")])],"isStart":false});
            var Q21;
            Q21=makeQuery(id+"F1.opExtrude","CAP_EDGE",EDGE,{"disambiguationData":[OSD([sQuery(id+"F0.wireOp",EDGE,"E104.5")])],"isStart":false});
            var Q22;
            Q22=makeQuery(id+"F1.opExtrude","CAP_EDGE",EDGE,{"disambiguationData":[OSD([sQuery(id+"F0.wireOp",EDGE,"E104.3")])],"isStart":false});
            var Q23;
            Q23=makeQuery(id+"F1.opExtrude","CAP_EDGE",EDGE,{"disambiguationData":[OSD([sQuery(id+"F0.wireOp",EDGE,"E104.2")])],"isStart":false});
            var Q24;
            Q24=makeQuery(id+"F1.opExtrude","CAP_EDGE",EDGE,{"disambiguationData":[OSD([sQuery(id+"F0.wireOp",EDGE,"E81.left")])],"isStart":false});
            var Q25;
            Q25=makeQuery(id+"F1.opExtrude","CAP_EDGE",EDGE,{"disambiguationData":[OSD([sQuery(id+"F0.wireOp",EDGE,"E81.bottom")])],"isStart":false});
            var Q26;
            Q26=makeQuery(id+"F1.opExtrude","CAP_EDGE",EDGE,{"disambiguationData":[OSD([sQuery(id+"F0.wireOp",EDGE,"E81.right")])],"isStart":false});
            var Q27;
            Q27=makeQuery(id+"F1.opExtrude","CAP_EDGE",EDGE,{"disambiguationData":[OSD([sQuery(id+"F0.wireOp",EDGE,"E83.left")])],"isStart":false});
            var Q28;
            Q28=makeQuery(id+"F1.opExtrude","CAP_EDGE",EDGE,{"disambiguationData":[OSD([sQuery(id+"F0.wireOp",EDGE,"E83.bottom")])],"isStart":false});
            var Q29;
            Q29=makeQuery(id+"F1.opExtrude","CAP_EDGE",EDGE,{"disambiguationData":[OSD([sQuery(id+"F0.wireOp",EDGE,"E83.right")])],"isStart":false});
            var Q30;
            Q30=makeQuery(id+"F1.opExtrude","CAP_EDGE",EDGE,{"disambiguationData":[OSD([sQuery(id+"F0.wireOp",EDGE,"E83.top")])],"isStart":false});
            var Q31;
            Q31=makeQuery(id+"F1.opExtrude","CAP_EDGE",EDGE,{"disambiguationData":[OSD([sQuery(id+"F0.wireOp",EDGE,"E81.top")])],"isStart":false});
            var Q32;
            Q32=makeQuery(id+"F1.opExtrude","CAP_EDGE",EDGE,{"disambiguationData":[OSD([sQuery(id+"F0.wireOp",EDGE,"E86.bottom")])],"isStart":false});
            var Q33;
            Q33=makeQuery(id+"F1.opExtrude","CAP_EDGE",EDGE,{"disambiguationData":[OSD([sQuery(id+"F0.wireOp",EDGE,"E86.left")])],"isStart":false});
            var Q34;
            Q34=makeQuery(id+"F1.opExtrude","CAP_EDGE",EDGE,{"disambiguationData":[OSD([sQuery(id+"F0.wireOp",EDGE,"E86.top")])],"isStart":false});
            var Q35;
            Q35=makeQuery(id+"F1.opExtrude","CAP_EDGE",EDGE,{"disambiguationData":[OSD([sQuery(id+"F0.wireOp",EDGE,"E86.right")])],"isStart":false});
            var Q36;
            Q36=makeQuery(id+"F1.opExtrude","CAP_EDGE",EDGE,{"disambiguationData":[OSD([sQuery(id+"F0.wireOp",EDGE,"E106.5")])],"isStart":false});
            var Q37;
            Q37=makeQuery(id+"F1.opExtrude","CAP_EDGE",EDGE,{"disambiguationData":[OSD([sQuery(id+"F0.wireOp",EDGE,"E106.0")])],"isStart":false});
            var Q38;
            Q38=makeQuery(id+"F1.opExtrude","CAP_EDGE",EDGE,{"disambiguationData":[OSD([sQuery(id+"F0.wireOp",EDGE,"E106.1")])],"isStart":false});
            var Q39;
            Q39=makeQuery(id+"F1.opExtrude","CAP_EDGE",EDGE,{"disambiguationData":[OSD([sQuery(id+"F0.wireOp",EDGE,"E106.2")])],"isStart":false});
            var Q40;
            Q40=makeQuery(id+"F1.opExtrude","CAP_EDGE",EDGE,{"disambiguationData":[OSD([sQuery(id+"F0.wireOp",EDGE,"E106.4")])],"isStart":false});
            var Q41;
            Q41=makeQuery(id+"F1.opExtrude","CAP_EDGE",EDGE,{"disambiguationData":[OSD([sQuery(id+"F0.wireOp",EDGE,"E106.3")])],"isStart":false});
            var Q42;
            Q42=makeQuery(id+"F1.opExtrude","CAP_EDGE",EDGE,{"disambiguationData":[OSD([sQuery(id+"F0.wireOp",EDGE,"E107.3")])],"isStart":false});
            var Q43;
            Q43=makeQuery(id+"F1.opExtrude","CAP_EDGE",EDGE,{"disambiguationData":[OSD([sQuery(id+"F0.wireOp",EDGE,"E107.4")])],"isStart":false});
            var Q44;
            Q44=makeQuery(id+"F1.opExtrude","CAP_EDGE",EDGE,{"disambiguationData":[OSD([sQuery(id+"F0.wireOp",EDGE,"E107.1")])],"isStart":false});
            var Q45;
            Q45=makeQuery(id+"F1.opExtrude","CAP_EDGE",EDGE,{"disambiguationData":[OSD([sQuery(id+"F0.wireOp",EDGE,"E107.2")])],"isStart":false});
            var Q46;
            Q46=makeQuery(id+"F1.opExtrude","CAP_EDGE",EDGE,{"disambiguationData":[OSD([sQuery(id+"F0.wireOp",EDGE,"E107.5")])],"isStart":false});
            var Q47;
            Q47=makeQuery(id+"F1.opExtrude","CAP_EDGE",EDGE,{"disambiguationData":[OSD([sQuery(id+"F0.wireOp",EDGE,"E107.0")])],"isStart":false});
            var Q48;
            Q48=makeQuery(id+"F1.opExtrude","CAP_EDGE",EDGE,{"disambiguationData":[OSD([sQuery(id+"F0.wireOp",EDGE,"E108.0")])],"isStart":false});
            var Q49;
            Q49=makeQuery(id+"F1.opExtrude","CAP_EDGE",EDGE,{"disambiguationData":[OSD([sQuery(id+"F0.wireOp",EDGE,"E108.2")])],"isStart":false});
            var Q50;
            Q50=makeQuery(id+"F1.opExtrude","CAP_EDGE",EDGE,{"disambiguationData":[OSD([sQuery(id+"F0.wireOp",EDGE,"E108.1")])],"isStart":false});
            var Q51;
            Q51=makeQuery(id+"F1.opExtrude","CAP_EDGE",EDGE,{"disambiguationData":[OSD([sQuery(id+"F0.wireOp",EDGE,"E108.4")])],"isStart":false});
            var Q52;
            Q52=makeQuery(id+"F1.opExtrude","CAP_EDGE",EDGE,{"disambiguationData":[OSD([sQuery(id+"F0.wireOp",EDGE,"E108.5")])],"isStart":false});
            var Q53;
            Q53=makeQuery(id+"F1.opExtrude","CAP_EDGE",EDGE,{"disambiguationData":[OSD([sQuery(id+"F0.wireOp",EDGE,"E108.3")])],"isStart":false});
            var Q54;
            Q54=makeQuery(id+"F1.opExtrude","CAP_EDGE",EDGE,{"disambiguationData":[OSD([sQuery(id+"F0.wireOp",EDGE,"E14")])],"isStart":false});
            var Q55;
            Q55=makeQuery(id+"F1.opExtrude","CAP_EDGE",EDGE,{"disambiguationData":[OSD([sQuery(id+"F0.wireOp",EDGE,"E16")])],"isStart":false});
            var Q56;
            Q56=makeQuery(id+"F1.opExtrude","CAP_EDGE",EDGE,{"disambiguationData":[OSD([sQuery(id+"F0.wireOp",EDGE,"E18")])],"isStart":false});
            var Q57;
            Q57=makeQuery(id+"F1.opExtrude","CAP_EDGE",EDGE,{"disambiguationData":[OSD([sQuery(id+"F0.wireOp",EDGE,"E20")])],"isStart":false});
            var Q58;
            Q58=makeQuery(id+"F1.opExtrude","CAP_EDGE",EDGE,{"disambiguationData":[OSD([sQuery(id+"F0.wireOp",EDGE,"E22")])],"isStart":false});
            var Q59;
            Q59=makeQuery(id+"F1.opExtrude","CAP_EDGE",EDGE,{"disambiguationData":[OSD([sQuery(id+"F0.wireOp",EDGE,"E24")])],"isStart":false});
            var Q60;
            Q60=makeQuery(id+"F1.opExtrude","CAP_EDGE",EDGE,{"disambiguationData":[OSD([sQuery(id+"F0.wireOp",EDGE,"E26")])],"isStart":false});
            var Q61;
            Q61=makeQuery(id+"F1.opExtrude","CAP_EDGE",EDGE,{"disambiguationData":[OSD([sQuery(id+"F0.wireOp",EDGE,"E28")])],"isStart":false});
            var Q62;
            Q62=makeQuery(id+"F1.opExtrude","CAP_EDGE",EDGE,{"disambiguationData":[OSD([sQuery(id+"F0.wireOp",EDGE,"E54")])],"isStart":false});
            var Q63;
            Q63=makeQuery(id+"F1.opExtrude","CAP_EDGE",EDGE,{"disambiguationData":[OSD([sQuery(id+"F0.wireOp",EDGE,"E52")])],"isStart":false});
            var Q64;
            Q64=makeQuery(id+"F1.opExtrude","CAP_EDGE",EDGE,{"disambiguationData":[OSD([sQuery(id+"F0.wireOp",EDGE,"E50")])],"isStart":false});
            var Q65;
            Q65=makeQuery(id+"F1.opExtrude","CAP_EDGE",EDGE,{"disambiguationData":[OSD([sQuery(id+"F0.wireOp",EDGE,"E56")])],"isStart":false});
            var Q66;
            Q66=makeQuery(id+"F1.opExtrude","CAP_EDGE",EDGE,{"disambiguationData":[OSD([sQuery(id+"F0.wireOp",EDGE,"E58")])],"isStart":false});
            var Q67;
            Q67=makeQuery(id+"F1.opExtrude","CAP_EDGE",EDGE,{"disambiguationData":[OSD([sQuery(id+"F0.wireOp",EDGE,"E60")])],"isStart":false});
            var Q68;
            Q68=makeQuery(id+"F1.opExtrude","CAP_EDGE",EDGE,{"disambiguationData":[OSD([sQuery(id+"F0.wireOp",EDGE,"E62")])],"isStart":false});
            var Q69;
            Q69=makeQuery(id+"F1.opExtrude","CAP_EDGE",EDGE,{"disambiguationData":[OSD([sQuery(id+"F0.wireOp",EDGE,"E64")])],"isStart":false});
            var Q70;
            Q70=makeQuery(id+"F1.opExtrude","CAP_EDGE",EDGE,{"disambiguationData":[OSD([sQuery(id+"F0.wireOp",EDGE,"E66")])],"isStart":false});
            var Q71;
            Q71=makeQuery(id+"F1.opExtrude","CAP_EDGE",EDGE,{"disambiguationData":[OSD([sQuery(id+"F0.wireOp",EDGE,"E68")])],"isStart":false});
            var Q72;
            Q72=makeQuery(id+"F1.opExtrude","CAP_EDGE",EDGE,{"disambiguationData":[OSD([sQuery(id+"F0.wireOp",EDGE,"E2")])],"isStart":false});
            var Q73;
            Q73=makeQuery(id+"F1.opExtrude","CAP_EDGE",EDGE,{"disambiguationData":[OSD([sQuery(id+"F0.wireOp",EDGE,"E4")])],"isStart":false});
            var Q74;
            Q74=makeQuery(id+"F1.opExtrude","CAP_EDGE",EDGE,{"disambiguationData":[OSD([sQuery(id+"F0.wireOp",EDGE,"E6")])],"isStart":false});
            var Q75;
            Q75=makeQuery(id+"F1.opExtrude","CAP_EDGE",EDGE,{"disambiguationData":[OSD([sQuery(id+"F0.wireOp",EDGE,"E8")])],"isStart":false});
            var Q76;
            Q76=makeQuery(id+"F1.opExtrude","CAP_EDGE",EDGE,{"disambiguationData":[OSD([sQuery(id+"F0.wireOp",EDGE,"E10")])],"isStart":false});
            var Q77;
            Q77=makeQuery(id+"F1.opExtrude","CAP_EDGE",EDGE,{"disambiguationData":[OSD([sQuery(id+"F0.wireOp",EDGE,"E12")])],"isStart":false});
            chamfer(context, id + "F6", {"entities" : qUnion([Q0, Q1, Q2, Q3, Q4, Q5, Q6, Q7, Q8, Q9, Q10, Q11, Q12, Q13, Q14, Q15, Q16, Q17, Q18, Q19, Q20, Q21, Q22, Q23, Q24, Q25, Q26, Q27, Q28, Q29, Q30, Q31, Q32, Q33, Q34, Q35, Q36, Q37, Q38, Q39, Q40, Q41, Q42, Q43, Q44, Q45, Q46, Q47, Q48, Q49, Q50, Q51, Q52, Q53, Q54, Q55, Q56, Q57, Q58, Q59, Q60, Q61, Q62, Q63, Q64, Q65, Q66, Q67, Q68, Q69, Q70, Q71, Q72, Q73, Q74, Q75, Q76, Q77]), "width" : 1 * mm, "tangentPropagation" : true});
        }
        {
            var Q0;
            {var subQ0=sQuery(id+"F0.wireOp",EDGE,"E102.4");Q0=makeQuery(id+"F6.opChamfer","BLEND_EDGE",EDGE,{"blendedFrom":[makeQuery(id+"F1.opExtrude","CAP_EDGE",EDGE,{"disambiguationData":[OSD([subQ0])],"isStart":false}),makeQuery(id+"F1.opExtrude","SWEPT_FACE",FACE,{"disambiguationData":[OSD([subQ0])]})],"blendedInto":[makeQuery(id+"F1.opExtrude","SWEPT_FACE",FACE,{"disambiguationData":[OSD([subQ0])]})]});}
            var Q1;
            {var subQ0=sQuery(id+"F0.wireOp",EDGE,"E102.5");Q1=makeQuery(id+"F6.opChamfer","BLEND_EDGE",EDGE,{"blendedFrom":[makeQuery(id+"F1.opExtrude","CAP_EDGE",EDGE,{"disambiguationData":[OSD([subQ0])],"isStart":false}),makeQuery(id+"F1.opExtrude","SWEPT_FACE",FACE,{"disambiguationData":[OSD([subQ0])]})],"blendedInto":[makeQuery(id+"F1.opExtrude","SWEPT_FACE",FACE,{"disambiguationData":[OSD([subQ0])]})]});}
            var Q2;
            {var subQ0=sQuery(id+"F0.wireOp",EDGE,"E102.3");Q2=makeQuery(id+"F6.opChamfer","BLEND_EDGE",EDGE,{"blendedFrom":[makeQuery(id+"F1.opExtrude","CAP_EDGE",EDGE,{"disambiguationData":[OSD([subQ0])],"isStart":false}),makeQuery(id+"F1.opExtrude","SWEPT_FACE",FACE,{"disambiguationData":[OSD([subQ0])]})],"blendedInto":[makeQuery(id+"F1.opExtrude","SWEPT_FACE",FACE,{"disambiguationData":[OSD([subQ0])]})]});}
            var Q3;
            {var subQ0=sQuery(id+"F0.wireOp",EDGE,"E103.4");Q3=makeQuery(id+"F6.opChamfer","BLEND_EDGE",EDGE,{"blendedFrom":[makeQuery(id+"F1.opExtrude","CAP_EDGE",EDGE,{"disambiguationData":[OSD([subQ0])],"isStart":false}),makeQuery(id+"F1.opExtrude","SWEPT_FACE",FACE,{"disambiguationData":[OSD([subQ0])]})],"blendedInto":[makeQuery(id+"F1.opExtrude","SWEPT_FACE",FACE,{"disambiguationData":[OSD([subQ0])]})]});}
            var Q4;
            {var subQ0=sQuery(id+"F0.wireOp",EDGE,"E103.5");Q4=makeQuery(id+"F6.opChamfer","BLEND_EDGE",EDGE,{"blendedFrom":[makeQuery(id+"F1.opExtrude","CAP_EDGE",EDGE,{"disambiguationData":[OSD([subQ0])],"isStart":false}),makeQuery(id+"F1.opExtrude","SWEPT_FACE",FACE,{"disambiguationData":[OSD([subQ0])]})],"blendedInto":[makeQuery(id+"F1.opExtrude","SWEPT_FACE",FACE,{"disambiguationData":[OSD([subQ0])]})]});}
            var Q5;
            {var subQ0=sQuery(id+"F0.wireOp",EDGE,"E103.0");Q5=makeQuery(id+"F6.opChamfer","BLEND_EDGE",EDGE,{"blendedFrom":[makeQuery(id+"F1.opExtrude","CAP_EDGE",EDGE,{"disambiguationData":[OSD([subQ0])],"isStart":false}),makeQuery(id+"F1.opExtrude","SWEPT_FACE",FACE,{"disambiguationData":[OSD([subQ0])]})],"blendedInto":[makeQuery(id+"F1.opExtrude","SWEPT_FACE",FACE,{"disambiguationData":[OSD([subQ0])]})]});}
            var Q6;
            {var subQ0=sQuery(id+"F0.wireOp",EDGE,"E103.3");Q6=makeQuery(id+"F6.opChamfer","BLEND_EDGE",EDGE,{"blendedFrom":[makeQuery(id+"F1.opExtrude","CAP_EDGE",EDGE,{"disambiguationData":[OSD([subQ0])],"isStart":false}),makeQuery(id+"F1.opExtrude","SWEPT_FACE",FACE,{"disambiguationData":[OSD([subQ0])]})],"blendedInto":[makeQuery(id+"F1.opExtrude","SWEPT_FACE",FACE,{"disambiguationData":[OSD([subQ0])]})]});}
            var Q7;
            {var subQ0=sQuery(id+"F0.wireOp",EDGE,"E103.2");Q7=makeQuery(id+"F6.opChamfer","BLEND_EDGE",EDGE,{"blendedFrom":[makeQuery(id+"F1.opExtrude","CAP_EDGE",EDGE,{"disambiguationData":[OSD([subQ0])],"isStart":false}),makeQuery(id+"F1.opExtrude","SWEPT_FACE",FACE,{"disambiguationData":[OSD([subQ0])]})],"blendedInto":[makeQuery(id+"F1.opExtrude","SWEPT_FACE",FACE,{"disambiguationData":[OSD([subQ0])]})]});}
            var Q8;
            {var subQ0=sQuery(id+"F0.wireOp",EDGE,"E104.4");Q8=makeQuery(id+"F6.opChamfer","BLEND_EDGE",EDGE,{"blendedFrom":[makeQuery(id+"F1.opExtrude","CAP_EDGE",EDGE,{"disambiguationData":[OSD([subQ0])],"isStart":false}),makeQuery(id+"F1.opExtrude","SWEPT_FACE",FACE,{"disambiguationData":[OSD([subQ0])]})],"blendedInto":[makeQuery(id+"F1.opExtrude","SWEPT_FACE",FACE,{"disambiguationData":[OSD([subQ0])]})]});}
            var Q9;
            {var subQ0=sQuery(id+"F0.wireOp",EDGE,"E104.5");Q9=makeQuery(id+"F6.opChamfer","BLEND_EDGE",EDGE,{"blendedFrom":[makeQuery(id+"F1.opExtrude","CAP_EDGE",EDGE,{"disambiguationData":[OSD([subQ0])],"isStart":false}),makeQuery(id+"F1.opExtrude","SWEPT_FACE",FACE,{"disambiguationData":[OSD([subQ0])]})],"blendedInto":[makeQuery(id+"F1.opExtrude","SWEPT_FACE",FACE,{"disambiguationData":[OSD([subQ0])]})]});}
            var Q10;
            {var subQ0=sQuery(id+"F0.wireOp",EDGE,"E104.0");Q10=makeQuery(id+"F6.opChamfer","BLEND_EDGE",EDGE,{"blendedFrom":[makeQuery(id+"F1.opExtrude","CAP_EDGE",EDGE,{"disambiguationData":[OSD([subQ0])],"isStart":false}),makeQuery(id+"F1.opExtrude","SWEPT_FACE",FACE,{"disambiguationData":[OSD([subQ0])]})],"blendedInto":[makeQuery(id+"F1.opExtrude","SWEPT_FACE",FACE,{"disambiguationData":[OSD([subQ0])]})]});}
            var Q11;
            {var subQ0=sQuery(id+"F0.wireOp",EDGE,"E104.3");Q11=makeQuery(id+"F6.opChamfer","BLEND_EDGE",EDGE,{"blendedFrom":[makeQuery(id+"F1.opExtrude","CAP_EDGE",EDGE,{"disambiguationData":[OSD([subQ0])],"isStart":false}),makeQuery(id+"F1.opExtrude","SWEPT_FACE",FACE,{"disambiguationData":[OSD([subQ0])]})],"blendedInto":[makeQuery(id+"F1.opExtrude","SWEPT_FACE",FACE,{"disambiguationData":[OSD([subQ0])]})]});}
            var Q12;
            {var subQ0=sQuery(id+"F0.wireOp",EDGE,"E102.0");Q12=makeQuery(id+"F6.opChamfer","BLEND_EDGE",EDGE,{"blendedFrom":[makeQuery(id+"F1.opExtrude","CAP_EDGE",EDGE,{"disambiguationData":[OSD([subQ0])],"isStart":false}),makeQuery(id+"F1.opExtrude","SWEPT_FACE",FACE,{"disambiguationData":[OSD([subQ0])]})],"blendedInto":[makeQuery(id+"F1.opExtrude","SWEPT_FACE",FACE,{"disambiguationData":[OSD([subQ0])]})]});}
            var Q13;
            {var subQ0=sQuery(id+"F0.wireOp",EDGE,"E102.1");Q13=makeQuery(id+"F6.opChamfer","BLEND_EDGE",EDGE,{"blendedFrom":[makeQuery(id+"F1.opExtrude","CAP_EDGE",EDGE,{"disambiguationData":[OSD([subQ0])],"isStart":false}),makeQuery(id+"F1.opExtrude","SWEPT_FACE",FACE,{"disambiguationData":[OSD([subQ0])]})],"blendedInto":[makeQuery(id+"F1.opExtrude","SWEPT_FACE",FACE,{"disambiguationData":[OSD([subQ0])]})]});}
            var Q14;
            {var subQ0=sQuery(id+"F0.wireOp",EDGE,"E102.2");Q14=makeQuery(id+"F6.opChamfer","BLEND_EDGE",EDGE,{"blendedFrom":[makeQuery(id+"F1.opExtrude","CAP_EDGE",EDGE,{"disambiguationData":[OSD([subQ0])],"isStart":false}),makeQuery(id+"F1.opExtrude","SWEPT_FACE",FACE,{"disambiguationData":[OSD([subQ0])]})],"blendedInto":[makeQuery(id+"F1.opExtrude","SWEPT_FACE",FACE,{"disambiguationData":[OSD([subQ0])]})]});}
            var Q15;
            {var subQ0=sQuery(id+"F0.wireOp",EDGE,"E103.1");Q15=makeQuery(id+"F6.opChamfer","BLEND_EDGE",EDGE,{"blendedFrom":[makeQuery(id+"F1.opExtrude","CAP_EDGE",EDGE,{"disambiguationData":[OSD([subQ0])],"isStart":false}),makeQuery(id+"F1.opExtrude","SWEPT_FACE",FACE,{"disambiguationData":[OSD([subQ0])]})],"blendedInto":[makeQuery(id+"F1.opExtrude","SWEPT_FACE",FACE,{"disambiguationData":[OSD([subQ0])]})]});}
            var Q16;
            {var subQ0=sQuery(id+"F0.wireOp",EDGE,"E104.2");Q16=makeQuery(id+"F6.opChamfer","BLEND_EDGE",EDGE,{"blendedFrom":[makeQuery(id+"F1.opExtrude","CAP_EDGE",EDGE,{"disambiguationData":[OSD([subQ0])],"isStart":false}),makeQuery(id+"F1.opExtrude","SWEPT_FACE",FACE,{"disambiguationData":[OSD([subQ0])]})],"blendedInto":[makeQuery(id+"F1.opExtrude","SWEPT_FACE",FACE,{"disambiguationData":[OSD([subQ0])]})]});}
            var Q17;
            {var subQ0=sQuery(id+"F0.wireOp",EDGE,"E104.1");Q17=makeQuery(id+"F6.opChamfer","BLEND_EDGE",EDGE,{"blendedFrom":[makeQuery(id+"F1.opExtrude","CAP_EDGE",EDGE,{"disambiguationData":[OSD([subQ0])],"isStart":false}),makeQuery(id+"F1.opExtrude","SWEPT_FACE",FACE,{"disambiguationData":[OSD([subQ0])]})],"blendedInto":[makeQuery(id+"F1.opExtrude","SWEPT_FACE",FACE,{"disambiguationData":[OSD([subQ0])]})]});}
            var Q18;
            {var subQ0=sQuery(id+"F0.wireOp",EDGE,"E105.3");Q18=makeQuery(id+"F6.opChamfer","BLEND_EDGE",EDGE,{"blendedFrom":[makeQuery(id+"F1.opExtrude","CAP_EDGE",EDGE,{"disambiguationData":[OSD([subQ0])],"isStart":false}),makeQuery(id+"F1.opExtrude","SWEPT_FACE",FACE,{"disambiguationData":[OSD([subQ0])]})],"blendedInto":[makeQuery(id+"F1.opExtrude","SWEPT_FACE",FACE,{"disambiguationData":[OSD([subQ0])]})]});}
            var Q19;
            {var subQ0=sQuery(id+"F0.wireOp",EDGE,"E105.2");Q19=makeQuery(id+"F6.opChamfer","BLEND_EDGE",EDGE,{"blendedFrom":[makeQuery(id+"F1.opExtrude","CAP_EDGE",EDGE,{"disambiguationData":[OSD([subQ0])],"isStart":false}),makeQuery(id+"F1.opExtrude","SWEPT_FACE",FACE,{"disambiguationData":[OSD([subQ0])]})],"blendedInto":[makeQuery(id+"F1.opExtrude","SWEPT_FACE",FACE,{"disambiguationData":[OSD([subQ0])]})]});}
            var Q20;
            {var subQ0=sQuery(id+"F0.wireOp",EDGE,"E105.0");Q20=makeQuery(id+"F6.opChamfer","BLEND_EDGE",EDGE,{"blendedFrom":[makeQuery(id+"F1.opExtrude","CAP_EDGE",EDGE,{"disambiguationData":[OSD([subQ0])],"isStart":false}),makeQuery(id+"F1.opExtrude","SWEPT_FACE",FACE,{"disambiguationData":[OSD([subQ0])]})],"blendedInto":[makeQuery(id+"F1.opExtrude","SWEPT_FACE",FACE,{"disambiguationData":[OSD([subQ0])]})]});}
            var Q21;
            {var subQ0=sQuery(id+"F0.wireOp",EDGE,"E106.0");Q21=makeQuery(id+"F6.opChamfer","BLEND_EDGE",EDGE,{"blendedFrom":[makeQuery(id+"F1.opExtrude","CAP_EDGE",EDGE,{"disambiguationData":[OSD([subQ0])],"isStart":false}),makeQuery(id+"F1.opExtrude","SWEPT_FACE",FACE,{"disambiguationData":[OSD([subQ0])]})],"blendedInto":[makeQuery(id+"F1.opExtrude","SWEPT_FACE",FACE,{"disambiguationData":[OSD([subQ0])]})]});}
            var Q22;
            {var subQ0=sQuery(id+"F0.wireOp",EDGE,"E106.1");Q22=makeQuery(id+"F6.opChamfer","BLEND_EDGE",EDGE,{"blendedFrom":[makeQuery(id+"F1.opExtrude","CAP_EDGE",EDGE,{"disambiguationData":[OSD([subQ0])],"isStart":false}),makeQuery(id+"F1.opExtrude","SWEPT_FACE",FACE,{"disambiguationData":[OSD([subQ0])]})],"blendedInto":[makeQuery(id+"F1.opExtrude","SWEPT_FACE",FACE,{"disambiguationData":[OSD([subQ0])]})]});}
            var Q23;
            {var subQ0=sQuery(id+"F0.wireOp",EDGE,"E106.2");Q23=makeQuery(id+"F6.opChamfer","BLEND_EDGE",EDGE,{"blendedFrom":[makeQuery(id+"F1.opExtrude","CAP_EDGE",EDGE,{"disambiguationData":[OSD([subQ0])],"isStart":false}),makeQuery(id+"F1.opExtrude","SWEPT_FACE",FACE,{"disambiguationData":[OSD([subQ0])]})],"blendedInto":[makeQuery(id+"F1.opExtrude","SWEPT_FACE",FACE,{"disambiguationData":[OSD([subQ0])]})]});}
            var Q24;
            {var subQ0=sQuery(id+"F0.wireOp",EDGE,"E105.1");Q24=makeQuery(id+"F6.opChamfer","BLEND_EDGE",EDGE,{"blendedFrom":[makeQuery(id+"F1.opExtrude","CAP_EDGE",EDGE,{"disambiguationData":[OSD([subQ0])],"isStart":false}),makeQuery(id+"F1.opExtrude","SWEPT_FACE",FACE,{"disambiguationData":[OSD([subQ0])]})],"blendedInto":[makeQuery(id+"F1.opExtrude","SWEPT_FACE",FACE,{"disambiguationData":[OSD([subQ0])]})]});}
            var Q25;
            {var subQ0=sQuery(id+"F0.wireOp",EDGE,"E105.4");Q25=makeQuery(id+"F6.opChamfer","BLEND_EDGE",EDGE,{"blendedFrom":[makeQuery(id+"F1.opExtrude","CAP_EDGE",EDGE,{"disambiguationData":[OSD([subQ0])],"isStart":false}),makeQuery(id+"F1.opExtrude","SWEPT_FACE",FACE,{"disambiguationData":[OSD([subQ0])]})],"blendedInto":[makeQuery(id+"F1.opExtrude","SWEPT_FACE",FACE,{"disambiguationData":[OSD([subQ0])]})]});}
            var Q26;
            {var subQ0=sQuery(id+"F0.wireOp",EDGE,"E105.5");Q26=makeQuery(id+"F6.opChamfer","BLEND_EDGE",EDGE,{"blendedFrom":[makeQuery(id+"F1.opExtrude","CAP_EDGE",EDGE,{"disambiguationData":[OSD([subQ0])],"isStart":false}),makeQuery(id+"F1.opExtrude","SWEPT_FACE",FACE,{"disambiguationData":[OSD([subQ0])]})],"blendedInto":[makeQuery(id+"F1.opExtrude","SWEPT_FACE",FACE,{"disambiguationData":[OSD([subQ0])]})]});}
            var Q27;
            {var subQ0=sQuery(id+"F0.wireOp",EDGE,"E106.5");Q27=makeQuery(id+"F6.opChamfer","BLEND_EDGE",EDGE,{"blendedFrom":[makeQuery(id+"F1.opExtrude","CAP_EDGE",EDGE,{"disambiguationData":[OSD([subQ0])],"isStart":false}),makeQuery(id+"F1.opExtrude","SWEPT_FACE",FACE,{"disambiguationData":[OSD([subQ0])]})],"blendedInto":[makeQuery(id+"F1.opExtrude","SWEPT_FACE",FACE,{"disambiguationData":[OSD([subQ0])]})]});}
            var Q28;
            {var subQ0=sQuery(id+"F0.wireOp",EDGE,"E106.4");Q28=makeQuery(id+"F6.opChamfer","BLEND_EDGE",EDGE,{"blendedFrom":[makeQuery(id+"F1.opExtrude","CAP_EDGE",EDGE,{"disambiguationData":[OSD([subQ0])],"isStart":false}),makeQuery(id+"F1.opExtrude","SWEPT_FACE",FACE,{"disambiguationData":[OSD([subQ0])]})],"blendedInto":[makeQuery(id+"F1.opExtrude","SWEPT_FACE",FACE,{"disambiguationData":[OSD([subQ0])]})]});}
            var Q29;
            {var subQ0=sQuery(id+"F0.wireOp",EDGE,"E106.3");Q29=makeQuery(id+"F6.opChamfer","BLEND_EDGE",EDGE,{"blendedFrom":[makeQuery(id+"F1.opExtrude","CAP_EDGE",EDGE,{"disambiguationData":[OSD([subQ0])],"isStart":false}),makeQuery(id+"F1.opExtrude","SWEPT_FACE",FACE,{"disambiguationData":[OSD([subQ0])]})],"blendedInto":[makeQuery(id+"F1.opExtrude","SWEPT_FACE",FACE,{"disambiguationData":[OSD([subQ0])]})]});}
            var Q30;
            {var subQ0=sQuery(id+"F0.wireOp",EDGE,"E107.4");Q30=makeQuery(id+"F6.opChamfer","BLEND_EDGE",EDGE,{"blendedFrom":[makeQuery(id+"F1.opExtrude","CAP_EDGE",EDGE,{"disambiguationData":[OSD([subQ0])],"isStart":false}),makeQuery(id+"F1.opExtrude","SWEPT_FACE",FACE,{"disambiguationData":[OSD([subQ0])]})],"blendedInto":[makeQuery(id+"F1.opExtrude","SWEPT_FACE",FACE,{"disambiguationData":[OSD([subQ0])]})]});}
            var Q31;
            {var subQ0=sQuery(id+"F0.wireOp",EDGE,"E107.3");Q31=makeQuery(id+"F6.opChamfer","BLEND_EDGE",EDGE,{"blendedFrom":[makeQuery(id+"F1.opExtrude","CAP_EDGE",EDGE,{"disambiguationData":[OSD([subQ0])],"isStart":false}),makeQuery(id+"F1.opExtrude","SWEPT_FACE",FACE,{"disambiguationData":[OSD([subQ0])]})],"blendedInto":[makeQuery(id+"F1.opExtrude","SWEPT_FACE",FACE,{"disambiguationData":[OSD([subQ0])]})]});}
            var Q32;
            {var subQ0=sQuery(id+"F0.wireOp",EDGE,"E107.5");Q32=makeQuery(id+"F6.opChamfer","BLEND_EDGE",EDGE,{"blendedFrom":[makeQuery(id+"F1.opExtrude","CAP_EDGE",EDGE,{"disambiguationData":[OSD([subQ0])],"isStart":false}),makeQuery(id+"F1.opExtrude","SWEPT_FACE",FACE,{"disambiguationData":[OSD([subQ0])]})],"blendedInto":[makeQuery(id+"F1.opExtrude","SWEPT_FACE",FACE,{"disambiguationData":[OSD([subQ0])]})]});}
            var Q33;
            {var subQ0=sQuery(id+"F0.wireOp",EDGE,"E107.0");Q33=makeQuery(id+"F6.opChamfer","BLEND_EDGE",EDGE,{"blendedFrom":[makeQuery(id+"F1.opExtrude","CAP_EDGE",EDGE,{"disambiguationData":[OSD([subQ0])],"isStart":false}),makeQuery(id+"F1.opExtrude","SWEPT_FACE",FACE,{"disambiguationData":[OSD([subQ0])]})],"blendedInto":[makeQuery(id+"F1.opExtrude","SWEPT_FACE",FACE,{"disambiguationData":[OSD([subQ0])]})]});}
            var Q34;
            {var subQ0=sQuery(id+"F0.wireOp",EDGE,"E107.1");Q34=makeQuery(id+"F6.opChamfer","BLEND_EDGE",EDGE,{"blendedFrom":[makeQuery(id+"F1.opExtrude","CAP_EDGE",EDGE,{"disambiguationData":[OSD([subQ0])],"isStart":false}),makeQuery(id+"F1.opExtrude","SWEPT_FACE",FACE,{"disambiguationData":[OSD([subQ0])]})],"blendedInto":[makeQuery(id+"F1.opExtrude","SWEPT_FACE",FACE,{"disambiguationData":[OSD([subQ0])]})]});}
            var Q35;
            {var subQ0=sQuery(id+"F0.wireOp",EDGE,"E107.2");Q35=makeQuery(id+"F6.opChamfer","BLEND_EDGE",EDGE,{"blendedFrom":[makeQuery(id+"F1.opExtrude","CAP_EDGE",EDGE,{"disambiguationData":[OSD([subQ0])],"isStart":false}),makeQuery(id+"F1.opExtrude","SWEPT_FACE",FACE,{"disambiguationData":[OSD([subQ0])]})],"blendedInto":[makeQuery(id+"F1.opExtrude","SWEPT_FACE",FACE,{"disambiguationData":[OSD([subQ0])]})]});}
            var Q36;
            {var subQ0=sQuery(id+"F0.wireOp",EDGE,"E108.2");Q36=makeQuery(id+"F6.opChamfer","BLEND_EDGE",EDGE,{"blendedFrom":[makeQuery(id+"F1.opExtrude","CAP_EDGE",EDGE,{"disambiguationData":[OSD([subQ0])],"isStart":false}),makeQuery(id+"F1.opExtrude","SWEPT_FACE",FACE,{"disambiguationData":[OSD([subQ0])]})],"blendedInto":[makeQuery(id+"F1.opExtrude","SWEPT_FACE",FACE,{"disambiguationData":[OSD([subQ0])]})]});}
            var Q37;
            {var subQ0=sQuery(id+"F0.wireOp",EDGE,"E108.1");Q37=makeQuery(id+"F6.opChamfer","BLEND_EDGE",EDGE,{"blendedFrom":[makeQuery(id+"F1.opExtrude","CAP_EDGE",EDGE,{"disambiguationData":[OSD([subQ0])],"isStart":false}),makeQuery(id+"F1.opExtrude","SWEPT_FACE",FACE,{"disambiguationData":[OSD([subQ0])]})],"blendedInto":[makeQuery(id+"F1.opExtrude","SWEPT_FACE",FACE,{"disambiguationData":[OSD([subQ0])]})]});}
            var Q38;
            {var subQ0=sQuery(id+"F0.wireOp",EDGE,"E108.0");Q38=makeQuery(id+"F6.opChamfer","BLEND_EDGE",EDGE,{"blendedFrom":[makeQuery(id+"F1.opExtrude","CAP_EDGE",EDGE,{"disambiguationData":[OSD([subQ0])],"isStart":false}),makeQuery(id+"F1.opExtrude","SWEPT_FACE",FACE,{"disambiguationData":[OSD([subQ0])]})],"blendedInto":[makeQuery(id+"F1.opExtrude","SWEPT_FACE",FACE,{"disambiguationData":[OSD([subQ0])]})]});}
            var Q39;
            {var subQ0=sQuery(id+"F0.wireOp",EDGE,"E108.5");Q39=makeQuery(id+"F6.opChamfer","BLEND_EDGE",EDGE,{"blendedFrom":[makeQuery(id+"F1.opExtrude","CAP_EDGE",EDGE,{"disambiguationData":[OSD([subQ0])],"isStart":false}),makeQuery(id+"F1.opExtrude","SWEPT_FACE",FACE,{"disambiguationData":[OSD([subQ0])]})],"blendedInto":[makeQuery(id+"F1.opExtrude","SWEPT_FACE",FACE,{"disambiguationData":[OSD([subQ0])]})]});}
            var Q40;
            {var subQ0=sQuery(id+"F0.wireOp",EDGE,"E108.4");Q40=makeQuery(id+"F6.opChamfer","BLEND_EDGE",EDGE,{"blendedFrom":[makeQuery(id+"F1.opExtrude","CAP_EDGE",EDGE,{"disambiguationData":[OSD([subQ0])],"isStart":false}),makeQuery(id+"F1.opExtrude","SWEPT_FACE",FACE,{"disambiguationData":[OSD([subQ0])]})],"blendedInto":[makeQuery(id+"F1.opExtrude","SWEPT_FACE",FACE,{"disambiguationData":[OSD([subQ0])]})]});}
            var Q41;
            {var subQ0=sQuery(id+"F0.wireOp",EDGE,"E108.3");Q41=makeQuery(id+"F6.opChamfer","BLEND_EDGE",EDGE,{"blendedFrom":[makeQuery(id+"F1.opExtrude","CAP_EDGE",EDGE,{"disambiguationData":[OSD([subQ0])],"isStart":false}),makeQuery(id+"F1.opExtrude","SWEPT_FACE",FACE,{"disambiguationData":[OSD([subQ0])]})],"blendedInto":[makeQuery(id+"F1.opExtrude","SWEPT_FACE",FACE,{"disambiguationData":[OSD([subQ0])]})]});}
            fillet(context, id + "F7", {"entities" : qUnion([Q0, Q1, Q2, Q3, Q4, Q5, Q6, Q7, Q8, Q9, Q10, Q11, Q12, Q13, Q14, Q15, Q16, Q17, Q18, Q19, Q20, Q21, Q22, Q23, Q24, Q25, Q26, Q27, Q28, Q29, Q30, Q31, Q32, Q33, Q34, Q35, Q36, Q37, Q38, Q39, Q40, Q41]), "radius" : 1 * mm, "tangentPropagation" : true, "allowEdgeOverflow" : false});
        }
        {
            var Q0;
            {var subQ9=sQuery(id+"F0.wireOp",EDGE,"E0.bottom");Q0=makeQuery(id+"F0.imprint","IMPRINT",FACE,{"disambiguationData":[TD([[makeQuery(id+"F0.imprint","IMPRINT",EDGE,{"derivedFrom":subQ9}),-1.0]])]});}
            var sketch = newSketch(context, id + "F8", { "sketchPlane" : qUnion([Q0])});
            skLineSegment(sketch, "E117.bottom", {"start": v(-72.33, 59.43) * mm, "end": v(68.26, 59.43) * mm});
            skLineSegment(sketch, "E117.top", {"start": v(-72.33, 53.65) * mm, "end": v(68.26, 53.65) * mm});
            skLineSegment(sketch, "E117.left", {"start": v(-72.33, 59.43) * mm, "end": v(-72.33, 53.65) * mm});
            skLineSegment(sketch, "E117.right", {"start": v(68.26, 59.43) * mm, "end": v(68.26, 53.65) * mm});
            skLineSegment(sketch, "E118.bottom", {"start": v(-73.05, 25.24) * mm, "end": v(72.21, 25.24) * mm});
            skLineSegment(sketch, "E118.top", {"start": v(-73.05, 19.53) * mm, "end": v(72.21, 19.53) * mm});
            skLineSegment(sketch, "E118.left", {"start": v(-73.05, 25.24) * mm, "end": v(-73.05, 19.53) * mm});
            skLineSegment(sketch, "E118.right", {"start": v(72.21, 25.24) * mm, "end": v(72.21, 19.53) * mm});
            skLineSegment(sketch, "E119.bottom", {"start": v(-54.34, -11.15) * mm, "end": v(68.26, -11.15) * mm});
            skLineSegment(sketch, "E119.top", {"start": v(-54.34, -6.53) * mm, "end": v(68.26, -6.53) * mm});
            skLineSegment(sketch, "E119.left", {"start": v(-54.34, -11.15) * mm, "end": v(-54.34, -6.53) * mm});
            skLineSegment(sketch, "E119.right", {"start": v(68.26, -11.15) * mm, "end": v(68.26, -6.53) * mm});
            skLineSegment(sketch, "E120.bottom", {"start": v(-77.29, -51.41) * mm, "end": v(76.71, -51.41) * mm});
            skLineSegment(sketch, "E120.top", {"start": v(-77.29, -58.11) * mm, "end": v(76.71, -58.11) * mm});
            skLineSegment(sketch, "E120.left", {"start": v(-77.29, -51.41) * mm, "end": v(-77.29, -58.11) * mm});
            skLineSegment(sketch, "E120.right", {"start": v(76.71, -51.41) * mm, "end": v(76.71, -58.11) * mm});
            skSolve(sketch);
        }
        {
            var Q0;
            Q0=makeQuery(id+"F8.imprint","IMPRINT",FACE,{"disambiguationData":[TD([[makeQuery(id+"F8.imprint","IMPRINT",EDGE,{"derivedFrom":makeQuery(id+"F0.imprint","IMPRINT",EDGE,{"derivedFrom":sQuery(id+"F0.wireOp",EDGE,"E31.sketch_text.stroke-0")})}),-1.0]])]});
            var Q1;
            Q1=makeQuery(id+"F8.imprint","IMPRINT",FACE,{"disambiguationData":[TD([[makeQuery(id+"F8.imprint","IMPRINT",EDGE,{"derivedFrom":makeQuery(id+"F0.imprint","IMPRINT",EDGE,{"derivedFrom":sQuery(id+"F0.wireOp",EDGE,"E31.sketch_text.stroke-10")})}),-1.0]])]});
            var Q2;
            Q2=makeQuery(id+"F8.imprint","IMPRINT",FACE,{"disambiguationData":[TD([[makeQuery(id+"F8.imprint","IMPRINT",EDGE,{"derivedFrom":makeQuery(id+"F0.imprint","IMPRINT",EDGE,{"derivedFrom":sQuery(id+"F0.wireOp",EDGE,"E32.sketch_text.stroke-0")})}),-1.0]])]});
            var Q3;
            Q3=makeQuery(id+"F8.imprint","IMPRINT",FACE,{"disambiguationData":[TD([[makeQuery(id+"F8.imprint","IMPRINT",EDGE,{"derivedFrom":makeQuery(id+"F0.imprint","IMPRINT",EDGE,{"derivedFrom":sQuery(id+"F0.wireOp",EDGE,"E32.sketch_text.stroke-24")})}),-1.0]])]});
            var Q4;
            Q4=makeQuery(id+"F8.imprint","IMPRINT",FACE,{"disambiguationData":[TD([[makeQuery(id+"F8.imprint","IMPRINT",EDGE,{"derivedFrom":makeQuery(id+"F0.imprint","IMPRINT",EDGE,{"derivedFrom":sQuery(id+"F0.wireOp",EDGE,"E33.sketch_text.stroke-0")})}),-1.0]])]});
            var Q5;
            Q5=makeQuery(id+"F8.imprint","IMPRINT",FACE,{"disambiguationData":[TD([[makeQuery(id+"F8.imprint","IMPRINT",EDGE,{"derivedFrom":makeQuery(id+"F0.imprint","IMPRINT",EDGE,{"derivedFrom":sQuery(id+"F0.wireOp",EDGE,"E33.sketch_text.stroke-24")})}),-1.0]])]});
            var Q6;
            Q6=makeQuery(id+"F8.imprint","IMPRINT",FACE,{"disambiguationData":[TD([[makeQuery(id+"F8.imprint","IMPRINT",EDGE,{"derivedFrom":makeQuery(id+"F0.imprint","IMPRINT",EDGE,{"derivedFrom":sQuery(id+"F0.wireOp",EDGE,"E34.sketch_text.stroke-0")})}),-1.0]])]});
            var Q7;
            Q7=makeQuery(id+"F8.imprint","IMPRINT",FACE,{"disambiguationData":[TD([[makeQuery(id+"F8.imprint","IMPRINT",EDGE,{"derivedFrom":makeQuery(id+"F0.imprint","IMPRINT",EDGE,{"derivedFrom":sQuery(id+"F0.wireOp",EDGE,"E34.sketch_text.stroke-24")})}),-1.0]])]});
            var Q8;
            Q8=makeQuery(id+"F8.imprint","IMPRINT",FACE,{"disambiguationData":[TD([[makeQuery(id+"F8.imprint","IMPRINT",EDGE,{"derivedFrom":makeQuery(id+"F0.imprint","IMPRINT",EDGE,{"derivedFrom":sQuery(id+"F0.wireOp",EDGE,"E35.sketch_text.stroke-0")})}),-1.0]])]});
            var Q9;
            Q9=makeQuery(id+"F8.imprint","IMPRINT",FACE,{"disambiguationData":[TD([[makeQuery(id+"F8.imprint","IMPRINT",EDGE,{"derivedFrom":makeQuery(id+"F0.imprint","IMPRINT",EDGE,{"derivedFrom":sQuery(id+"F0.wireOp",EDGE,"E35.sketch_text.stroke-24")})}),-1.0]])]});
            var Q10;
            Q10=makeQuery(id+"F8.imprint","IMPRINT",FACE,{"disambiguationData":[TD([[makeQuery(id+"F8.imprint","IMPRINT",EDGE,{"derivedFrom":makeQuery(id+"F0.imprint","IMPRINT",EDGE,{"derivedFrom":sQuery(id+"F0.wireOp",EDGE,"E36.sketch_text.stroke-0")})}),-1.0]])]});
            var Q11;
            Q11=makeQuery(id+"F8.imprint","IMPRINT",FACE,{"disambiguationData":[TD([[makeQuery(id+"F8.imprint","IMPRINT",EDGE,{"derivedFrom":makeQuery(id+"F0.imprint","IMPRINT",EDGE,{"derivedFrom":sQuery(id+"F0.wireOp",EDGE,"E36.sketch_text.stroke-24")})}),-1.0]])]});
            var Q12;
            Q12=makeQuery(id+"F8.imprint","IMPRINT",FACE,{"disambiguationData":[TD([[makeQuery(id+"F8.imprint","IMPRINT",EDGE,{"derivedFrom":makeQuery(id+"F0.imprint","IMPRINT",EDGE,{"derivedFrom":sQuery(id+"F0.wireOp",EDGE,"E39.sketch_text.stroke-0")})}),-1.0]])]});
            var Q13;
            Q13=makeQuery(id+"F8.imprint","IMPRINT",FACE,{"disambiguationData":[TD([[makeQuery(id+"F8.imprint","IMPRINT",EDGE,{"derivedFrom":makeQuery(id+"F0.imprint","IMPRINT",EDGE,{"derivedFrom":sQuery(id+"F0.wireOp",EDGE,"E39.sketch_text.stroke-10")})}),-1.0]])]});
            var Q14;
            Q14=makeQuery(id+"F8.imprint","IMPRINT",FACE,{"disambiguationData":[TD([[makeQuery(id+"F8.imprint","IMPRINT",EDGE,{"derivedFrom":makeQuery(id+"F0.imprint","IMPRINT",EDGE,{"derivedFrom":sQuery(id+"F0.wireOp",EDGE,"E40.sketch_text.stroke-0")})}),-1.0]])]});
            var Q15;
            Q15=makeQuery(id+"F8.imprint","IMPRINT",FACE,{"disambiguationData":[TD([[makeQuery(id+"F8.imprint","IMPRINT",EDGE,{"derivedFrom":makeQuery(id+"F0.imprint","IMPRINT",EDGE,{"derivedFrom":sQuery(id+"F0.wireOp",EDGE,"E40.sketch_text.stroke-10")})}),-1.0]])]});
            var Q16;
            Q16=makeQuery(id+"F8.imprint","IMPRINT",FACE,{"disambiguationData":[TD([[makeQuery(id+"F8.imprint","IMPRINT",EDGE,{"derivedFrom":makeQuery(id+"F0.imprint","IMPRINT",EDGE,{"derivedFrom":sQuery(id+"F0.wireOp",EDGE,"E41.sketch_text.stroke-0")})}),-1.0]])]});
            var Q17;
            Q17=makeQuery(id+"F8.imprint","IMPRINT",FACE,{"disambiguationData":[TD([[makeQuery(id+"F8.imprint","IMPRINT",EDGE,{"derivedFrom":makeQuery(id+"F0.imprint","IMPRINT",EDGE,{"derivedFrom":sQuery(id+"F0.wireOp",EDGE,"E41.sketch_text.stroke-10")})}),-1.0]])]});
            var Q18;
            Q18=makeQuery(id+"F8.imprint","IMPRINT",FACE,{"disambiguationData":[TD([[makeQuery(id+"F8.imprint","IMPRINT",EDGE,{"derivedFrom":makeQuery(id+"F0.imprint","IMPRINT",EDGE,{"derivedFrom":sQuery(id+"F0.wireOp",EDGE,"E42.sketch_text.stroke-0")})}),-1.0]])]});
            var Q19;
            Q19=makeQuery(id+"F8.imprint","IMPRINT",FACE,{"disambiguationData":[TD([[makeQuery(id+"F8.imprint","IMPRINT",EDGE,{"derivedFrom":makeQuery(id+"F0.imprint","IMPRINT",EDGE,{"derivedFrom":sQuery(id+"F0.wireOp",EDGE,"E42.sketch_text.stroke-10")})}),-1.0]])]});
            var Q20;
            Q20=makeQuery(id+"F8.imprint","IMPRINT",FACE,{"disambiguationData":[TD([[makeQuery(id+"F8.imprint","IMPRINT",EDGE,{"derivedFrom":makeQuery(id+"F0.imprint","IMPRINT",EDGE,{"derivedFrom":sQuery(id+"F0.wireOp",EDGE,"E43.sketch_text.stroke-0")})}),-1.0]])]});
            var Q21;
            Q21=makeQuery(id+"F8.imprint","IMPRINT",FACE,{"disambiguationData":[TD([[makeQuery(id+"F8.imprint","IMPRINT",EDGE,{"derivedFrom":makeQuery(id+"F0.imprint","IMPRINT",EDGE,{"derivedFrom":sQuery(id+"F0.wireOp",EDGE,"E43.sketch_text.stroke-10")})}),-1.0]])]});
            var Q22;
            Q22=makeQuery(id+"F8.imprint","IMPRINT",FACE,{"disambiguationData":[TD([[makeQuery(id+"F8.imprint","IMPRINT",EDGE,{"derivedFrom":makeQuery(id+"F0.imprint","IMPRINT",EDGE,{"derivedFrom":sQuery(id+"F0.wireOp",EDGE,"E44.sketch_text.stroke-0")})}),-1.0]])]});
            var Q23;
            Q23=makeQuery(id+"F8.imprint","IMPRINT",FACE,{"disambiguationData":[TD([[makeQuery(id+"F8.imprint","IMPRINT",EDGE,{"derivedFrom":makeQuery(id+"F0.imprint","IMPRINT",EDGE,{"derivedFrom":sQuery(id+"F0.wireOp",EDGE,"E44.sketch_text.stroke-10")})}),-1.0]])]});
            var Q24;
            Q24=makeQuery(id+"F8.imprint","IMPRINT",FACE,{"disambiguationData":[TD([[makeQuery(id+"F8.imprint","IMPRINT",EDGE,{"derivedFrom":makeQuery(id+"F0.imprint","IMPRINT",EDGE,{"derivedFrom":sQuery(id+"F0.wireOp",EDGE,"E45.sketch_text.stroke-0")})}),-1.0]])]});
            var Q25;
            Q25=makeQuery(id+"F8.imprint","IMPRINT",FACE,{"disambiguationData":[TD([[makeQuery(id+"F8.imprint","IMPRINT",EDGE,{"derivedFrom":makeQuery(id+"F0.imprint","IMPRINT",EDGE,{"derivedFrom":sQuery(id+"F0.wireOp",EDGE,"E45.sketch_text.stroke-10")})}),-1.0]])]});
            var Q26;
            Q26=makeQuery(id+"F8.imprint","IMPRINT",FACE,{"disambiguationData":[TD([[makeQuery(id+"F8.imprint","IMPRINT",EDGE,{"derivedFrom":makeQuery(id+"F0.imprint","IMPRINT",EDGE,{"derivedFrom":sQuery(id+"F0.wireOp",EDGE,"E46.sketch_text.stroke-0")})}),-1.0]])]});
            var Q27;
            Q27=makeQuery(id+"F8.imprint","IMPRINT",FACE,{"disambiguationData":[TD([[makeQuery(id+"F8.imprint","IMPRINT",EDGE,{"derivedFrom":makeQuery(id+"F0.imprint","IMPRINT",EDGE,{"derivedFrom":sQuery(id+"F0.wireOp",EDGE,"E46.sketch_text.stroke-10")})}),-1.0]])]});
            var Q28;
            Q28=makeQuery(id+"F8.imprint","IMPRINT",FACE,{"disambiguationData":[TD([[makeQuery(id+"F8.imprint","IMPRINT",EDGE,{"derivedFrom":makeQuery(id+"F0.imprint","IMPRINT",EDGE,{"derivedFrom":sQuery(id+"F0.wireOp",EDGE,"E69.sketch_text.stroke-0")})}),-1.0]])]});
            var Q29;
            Q29=makeQuery(id+"F8.imprint","IMPRINT",FACE,{"disambiguationData":[TD([[makeQuery(id+"F8.imprint","IMPRINT",EDGE,{"derivedFrom":makeQuery(id+"F0.imprint","IMPRINT",EDGE,{"derivedFrom":sQuery(id+"F0.wireOp",EDGE,"E69.sketch_text.stroke-10")})}),-1.0]])]});
            var Q30;
            Q30=makeQuery(id+"F8.imprint","IMPRINT",FACE,{"disambiguationData":[TD([[makeQuery(id+"F8.imprint","IMPRINT",EDGE,{"derivedFrom":makeQuery(id+"F0.imprint","IMPRINT",EDGE,{"derivedFrom":sQuery(id+"F0.wireOp",EDGE,"E70.sketch_text.stroke-0")})}),-1.0]])]});
            var Q31;
            Q31=makeQuery(id+"F8.imprint","IMPRINT",FACE,{"disambiguationData":[TD([[makeQuery(id+"F8.imprint","IMPRINT",EDGE,{"derivedFrom":makeQuery(id+"F0.imprint","IMPRINT",EDGE,{"derivedFrom":sQuery(id+"F0.wireOp",EDGE,"E71.sketch_text.stroke-0")})}),-1.0]])]});
            var Q32;
            Q32=makeQuery(id+"F8.imprint","IMPRINT",FACE,{"disambiguationData":[TD([[makeQuery(id+"F8.imprint","IMPRINT",EDGE,{"derivedFrom":makeQuery(id+"F0.imprint","IMPRINT",EDGE,{"derivedFrom":sQuery(id+"F0.wireOp",EDGE,"E72.sketch_text.stroke-0")})}),-1.0]])]});
            var Q33;
            Q33=makeQuery(id+"F8.imprint","IMPRINT",FACE,{"disambiguationData":[TD([[makeQuery(id+"F8.imprint","IMPRINT",EDGE,{"derivedFrom":makeQuery(id+"F0.imprint","IMPRINT",EDGE,{"derivedFrom":sQuery(id+"F0.wireOp",EDGE,"E73.sketch_text.stroke-0")})}),-1.0]])]});
            var Q34;
            Q34=makeQuery(id+"F8.imprint","IMPRINT",FACE,{"disambiguationData":[TD([[makeQuery(id+"F8.imprint","IMPRINT",EDGE,{"derivedFrom":makeQuery(id+"F0.imprint","IMPRINT",EDGE,{"derivedFrom":sQuery(id+"F0.wireOp",EDGE,"E74.sketch_text.stroke-0")})}),-1.0]])]});
            var Q35;
            Q35=makeQuery(id+"F8.imprint","IMPRINT",FACE,{"disambiguationData":[TD([[makeQuery(id+"F8.imprint","IMPRINT",EDGE,{"derivedFrom":makeQuery(id+"F0.imprint","IMPRINT",EDGE,{"derivedFrom":sQuery(id+"F0.wireOp",EDGE,"E75.sketch_text.stroke-0")})}),-1.0]])]});
            var Q36;
            Q36=makeQuery(id+"F8.imprint","IMPRINT",FACE,{"disambiguationData":[TD([[makeQuery(id+"F8.imprint","IMPRINT",EDGE,{"derivedFrom":makeQuery(id+"F0.imprint","IMPRINT",EDGE,{"derivedFrom":sQuery(id+"F0.wireOp",EDGE,"E76.sketch_text.stroke-0")})}),-1.0]])]});
            var Q37;
            Q37=makeQuery(id+"F8.imprint","IMPRINT",FACE,{"disambiguationData":[TD([[makeQuery(id+"F8.imprint","IMPRINT",EDGE,{"derivedFrom":makeQuery(id+"F0.imprint","IMPRINT",EDGE,{"derivedFrom":sQuery(id+"F0.wireOp",EDGE,"E77.sketch_text.stroke-0")})}),-1.0]])]});
            var Q38;
            Q38=makeQuery(id+"F8.imprint","IMPRINT",FACE,{"disambiguationData":[TD([[makeQuery(id+"F8.imprint","IMPRINT",EDGE,{"derivedFrom":makeQuery(id+"F0.imprint","IMPRINT",EDGE,{"derivedFrom":sQuery(id+"F0.wireOp",EDGE,"E78.sketch_text.stroke-0")})}),-1.0]])]});
            var Q39;
            Q39=makeQuery(id+"F8.imprint","IMPRINT",FACE,{"disambiguationData":[TD([[makeQuery(id+"F8.imprint","IMPRINT",EDGE,{"derivedFrom":makeQuery(id+"F0.imprint","IMPRINT",EDGE,{"derivedFrom":sQuery(id+"F0.wireOp",EDGE,"E79.sketch_text.stroke-0")})}),-1.0]])]});
            var Q40;
            Q40=makeQuery(id+"F8.imprint","IMPRINT",FACE,{"disambiguationData":[TD([[makeQuery(id+"F8.imprint","IMPRINT",EDGE,{"derivedFrom":makeQuery(id+"F0.imprint","IMPRINT",EDGE,{"derivedFrom":sQuery(id+"F0.wireOp",EDGE,"E79.sketch_text.stroke-28")})}),-1.0]])]});
            var Q41;
            Q41=makeQuery(id+"F8.imprint","IMPRINT",FACE,{"disambiguationData":[TD([[makeQuery(id+"F8.imprint","IMPRINT",EDGE,{"derivedFrom":makeQuery(id+"F0.imprint","IMPRINT",EDGE,{"derivedFrom":sQuery(id+"F0.wireOp",EDGE,"E80.sketch_text.stroke-0")})}),-1.0]])]});
            var Q42;
            Q42=makeQuery(id+"F8.imprint","IMPRINT",FACE,{"disambiguationData":[TD([[makeQuery(id+"F8.imprint","IMPRINT",EDGE,{"derivedFrom":makeQuery(id+"F0.imprint","IMPRINT",EDGE,{"derivedFrom":sQuery(id+"F0.wireOp",EDGE,"E80.sketch_text.stroke-28")})}),-1.0]])]});
            var Q43;
            Q43=makeQuery(id+"F8.imprint","IMPRINT",FACE,{"disambiguationData":[TD([[makeQuery(id+"F8.imprint","IMPRINT",EDGE,{"derivedFrom":makeQuery(id+"F0.imprint","IMPRINT",EDGE,{"derivedFrom":sQuery(id+"F0.wireOp",EDGE,"E87.sketch_text.stroke-5")})}),-1.0]])]});
            var Q44;
            Q44=makeQuery(id+"F8.imprint","IMPRINT",FACE,{"disambiguationData":[TD([[makeQuery(id+"F8.imprint","IMPRINT",EDGE,{"derivedFrom":makeQuery(id+"F0.imprint","IMPRINT",EDGE,{"derivedFrom":sQuery(id+"F0.wireOp",EDGE,"E87.sketch_text.stroke-20")})}),-1.0]])]});
            var Q45;
            Q45=makeQuery(id+"F8.imprint","IMPRINT",FACE,{"disambiguationData":[TD([[makeQuery(id+"F8.imprint","IMPRINT",EDGE,{"derivedFrom":makeQuery(id+"F0.imprint","IMPRINT",EDGE,{"derivedFrom":sQuery(id+"F0.wireOp",EDGE,"E87.sketch_text.stroke-37")})}),-1.0]])]});
            var Q46;
            Q46=makeQuery(id+"F8.imprint","IMPRINT",FACE,{"disambiguationData":[TD([[makeQuery(id+"F8.imprint","IMPRINT",EDGE,{"derivedFrom":makeQuery(id+"F0.imprint","IMPRINT",EDGE,{"derivedFrom":sQuery(id+"F0.wireOp",EDGE,"E87.sketch_text.stroke-65")})}),-1.0]])]});
            var Q47;
            Q47=makeQuery(id+"F8.imprint","IMPRINT",FACE,{"disambiguationData":[TD([[makeQuery(id+"F8.imprint","IMPRINT",EDGE,{"derivedFrom":makeQuery(id+"F0.imprint","IMPRINT",EDGE,{"derivedFrom":sQuery(id+"F0.wireOp",EDGE,"E111.sketch_text.stroke-0")})}),-1.0]])]});
            var Q48;
            Q48=makeQuery(id+"F8.imprint","IMPRINT",FACE,{"disambiguationData":[TD([[makeQuery(id+"F8.imprint","IMPRINT",EDGE,{"derivedFrom":makeQuery(id+"F0.imprint","IMPRINT",EDGE,{"derivedFrom":sQuery(id+"F0.wireOp",EDGE,"E111.sketch_text.stroke-10")})}),-1.0]])]});
            var Q49;
            Q49=makeQuery(id+"F8.imprint","IMPRINT",FACE,{"disambiguationData":[TD([[makeQuery(id+"F8.imprint","IMPRINT",EDGE,{"derivedFrom":makeQuery(id+"F0.imprint","IMPRINT",EDGE,{"derivedFrom":sQuery(id+"F0.wireOp",EDGE,"E111.sketch_text.stroke-36")})}),-1.0]])]});
            var Q50;
            Q50=makeQuery(id+"F8.imprint","IMPRINT",FACE,{"disambiguationData":[TD([[makeQuery(id+"F8.imprint","IMPRINT",EDGE,{"derivedFrom":makeQuery(id+"F0.imprint","IMPRINT",EDGE,{"derivedFrom":sQuery(id+"F0.wireOp",EDGE,"E111.sketch_text.stroke-44")})}),-1.0]])]});
            var Q51;
            Q51=makeQuery(id+"F8.imprint","IMPRINT",FACE,{"disambiguationData":[TD([[makeQuery(id+"F8.imprint","IMPRINT",EDGE,{"derivedFrom":makeQuery(id+"F0.imprint","IMPRINT",EDGE,{"derivedFrom":sQuery(id+"F0.wireOp",EDGE,"E112.sketch_text.stroke-0")})}),-1.0]])]});
            var Q52;
            Q52=makeQuery(id+"F8.imprint","IMPRINT",FACE,{"disambiguationData":[TD([[makeQuery(id+"F8.imprint","IMPRINT",EDGE,{"derivedFrom":makeQuery(id+"F0.imprint","IMPRINT",EDGE,{"derivedFrom":sQuery(id+"F0.wireOp",EDGE,"E112.sketch_text.stroke-10")})}),-1.0]])]});
            var Q53;
            Q53=makeQuery(id+"F8.imprint","IMPRINT",FACE,{"disambiguationData":[TD([[makeQuery(id+"F8.imprint","IMPRINT",EDGE,{"derivedFrom":makeQuery(id+"F0.imprint","IMPRINT",EDGE,{"derivedFrom":sQuery(id+"F0.wireOp",EDGE,"E112.sketch_text.stroke-36")})}),-1.0]])]});
            var Q54;
            Q54=makeQuery(id+"F8.imprint","IMPRINT",FACE,{"disambiguationData":[TD([[makeQuery(id+"F8.imprint","IMPRINT",EDGE,{"derivedFrom":makeQuery(id+"F0.imprint","IMPRINT",EDGE,{"derivedFrom":sQuery(id+"F0.wireOp",EDGE,"E112.sketch_text.stroke-44")})}),-1.0]])]});
            var Q55;
            Q55=makeQuery(id+"F8.imprint","IMPRINT",FACE,{"disambiguationData":[TD([[makeQuery(id+"F8.imprint","IMPRINT",EDGE,{"derivedFrom":makeQuery(id+"F0.imprint","IMPRINT",EDGE,{"derivedFrom":sQuery(id+"F0.wireOp",EDGE,"E113.sketch_text.stroke-0")})}),-1.0]])]});
            var Q56;
            Q56=makeQuery(id+"F8.imprint","IMPRINT",FACE,{"disambiguationData":[TD([[makeQuery(id+"F8.imprint","IMPRINT",EDGE,{"derivedFrom":makeQuery(id+"F0.imprint","IMPRINT",EDGE,{"derivedFrom":sQuery(id+"F0.wireOp",EDGE,"E113.sketch_text.stroke-24")})}),-1.0]])]});
            var Q57;
            Q57=makeQuery(id+"F8.imprint","IMPRINT",FACE,{"disambiguationData":[TD([[makeQuery(id+"F8.imprint","IMPRINT",EDGE,{"derivedFrom":makeQuery(id+"F0.imprint","IMPRINT",EDGE,{"derivedFrom":sQuery(id+"F0.wireOp",EDGE,"E113.sketch_text.stroke-40")})}),-1.0]])]});
            var Q58;
            Q58=makeQuery(id+"F8.imprint","IMPRINT",FACE,{"disambiguationData":[TD([[makeQuery(id+"F8.imprint","IMPRINT",EDGE,{"derivedFrom":makeQuery(id+"F0.imprint","IMPRINT",EDGE,{"derivedFrom":sQuery(id+"F0.wireOp",EDGE,"E113.sketch_text.stroke-48")})}),-1.0]])]});
            var Q59;
            Q59=makeQuery(id+"F8.imprint","IMPRINT",FACE,{"disambiguationData":[TD([[makeQuery(id+"F8.imprint","IMPRINT",EDGE,{"derivedFrom":makeQuery(id+"F0.imprint","IMPRINT",EDGE,{"derivedFrom":sQuery(id+"F0.wireOp",EDGE,"E114.sketch_text.stroke-0")})}),-1.0]])]});
            var Q60;
            Q60=makeQuery(id+"F8.imprint","IMPRINT",FACE,{"disambiguationData":[TD([[makeQuery(id+"F8.imprint","IMPRINT",EDGE,{"derivedFrom":makeQuery(id+"F0.imprint","IMPRINT",EDGE,{"derivedFrom":sQuery(id+"F0.wireOp",EDGE,"E114.sketch_text.stroke-12")})}),-1.0]])]});
            var Q61;
            Q61=makeQuery(id+"F8.imprint","IMPRINT",FACE,{"disambiguationData":[TD([[makeQuery(id+"F8.imprint","IMPRINT",EDGE,{"derivedFrom":makeQuery(id+"F0.imprint","IMPRINT",EDGE,{"derivedFrom":sQuery(id+"F0.wireOp",EDGE,"E114.sketch_text.stroke-17")})}),-1.0]])]});
            var Q62;
            Q62=makeQuery(id+"F8.imprint","IMPRINT",FACE,{"disambiguationData":[TD([[makeQuery(id+"F8.imprint","IMPRINT",EDGE,{"derivedFrom":makeQuery(id+"F0.imprint","IMPRINT",EDGE,{"derivedFrom":sQuery(id+"F0.wireOp",EDGE,"E114.sketch_text.stroke-21")})}),-1.0]])]});
            var Q63;
            Q63=makeQuery(id+"F8.imprint","IMPRINT",FACE,{"disambiguationData":[TD([[makeQuery(id+"F8.imprint","IMPRINT",EDGE,{"derivedFrom":makeQuery(id+"F0.imprint","IMPRINT",EDGE,{"derivedFrom":sQuery(id+"F0.wireOp",EDGE,"E114.sketch_text.stroke-47")})}),-1.0]])]});
            var Q64;
            Q64=makeQuery(id+"F8.imprint","IMPRINT",FACE,{"disambiguationData":[TD([[makeQuery(id+"F8.imprint","IMPRINT",EDGE,{"derivedFrom":makeQuery(id+"F0.imprint","IMPRINT",EDGE,{"derivedFrom":sQuery(id+"F0.wireOp",EDGE,"E114.sketch_text.stroke-65")})}),-1.0]])]});
            var Q65;
            Q65=makeQuery(id+"F8.imprint","IMPRINT",FACE,{"disambiguationData":[TD([[makeQuery(id+"F8.imprint","IMPRINT",EDGE,{"derivedFrom":makeQuery(id+"F0.imprint","IMPRINT",EDGE,{"derivedFrom":sQuery(id+"F0.wireOp",EDGE,"E114.sketch_text.stroke-96")})}),-1.0]])]});
            var Q66;
            Q66=makeQuery(id+"F8.imprint","IMPRINT",FACE,{"disambiguationData":[TD([[makeQuery(id+"F8.imprint","IMPRINT",EDGE,{"derivedFrom":makeQuery(id+"F0.imprint","IMPRINT",EDGE,{"derivedFrom":sQuery(id+"F0.wireOp",EDGE,"E114.sketch_text.stroke-106")})}),-1.0]])]});
            var Q67;
            Q67=makeQuery(id+"F8.imprint","IMPRINT",FACE,{"disambiguationData":[TD([[makeQuery(id+"F8.imprint","IMPRINT",EDGE,{"derivedFrom":makeQuery(id+"F0.imprint","IMPRINT",EDGE,{"derivedFrom":sQuery(id+"F0.wireOp",EDGE,"E114.sketch_text.stroke-111")})}),-1.0]])]});
            var Q68;
            Q68=makeQuery(id+"F8.imprint","IMPRINT",FACE,{"disambiguationData":[TD([[makeQuery(id+"F8.imprint","IMPRINT",EDGE,{"derivedFrom":makeQuery(id+"F0.imprint","IMPRINT",EDGE,{"derivedFrom":sQuery(id+"F0.wireOp",EDGE,"E114.sketch_text.stroke-115")})}),-1.0]])]});
            var Q69;
            Q69=makeQuery(id+"F8.imprint","IMPRINT",FACE,{"disambiguationData":[TD([[makeQuery(id+"F8.imprint","IMPRINT",EDGE,{"derivedFrom":makeQuery(id+"F0.imprint","IMPRINT",EDGE,{"derivedFrom":sQuery(id+"F0.wireOp",EDGE,"E114.sketch_text.stroke-132")})}),-1.0]])]});
            var Q70;
            Q70=makeQuery(id+"F8.imprint","IMPRINT",FACE,{"disambiguationData":[TD([[makeQuery(id+"F8.imprint","IMPRINT",EDGE,{"derivedFrom":makeQuery(id+"F0.imprint","IMPRINT",EDGE,{"derivedFrom":sQuery(id+"F0.wireOp",EDGE,"E114.sketch_text.stroke-155")})}),-1.0]])]});
            var Q71;
            Q71=makeQuery(id+"F8.imprint","IMPRINT",FACE,{"disambiguationData":[TD([[makeQuery(id+"F8.imprint","IMPRINT",EDGE,{"derivedFrom":makeQuery(id+"F0.imprint","IMPRINT",EDGE,{"derivedFrom":sQuery(id+"F0.wireOp",EDGE,"E114.sketch_text.stroke-170")})}),-1.0]])]});
            var Q72;
            Q72=makeQuery(id+"F8.imprint","IMPRINT",FACE,{"disambiguationData":[TD([[makeQuery(id+"F8.imprint","IMPRINT",EDGE,{"derivedFrom":makeQuery(id+"F0.imprint","IMPRINT",EDGE,{"derivedFrom":sQuery(id+"F0.wireOp",EDGE,"E114.sketch_text.stroke-195")})}),-1.0]])]});
            var Q73;
            Q73=makeQuery(id+"F8.imprint","IMPRINT",FACE,{"disambiguationData":[TD([[makeQuery(id+"F8.imprint","IMPRINT",EDGE,{"derivedFrom":makeQuery(id+"F0.imprint","IMPRINT",EDGE,{"derivedFrom":sQuery(id+"F0.wireOp",EDGE,"E114.sketch_text.stroke-202")})}),-1.0]])]});
            var Q74;
            Q74=makeQuery(id+"F8.imprint","IMPRINT",FACE,{"disambiguationData":[TD([[makeQuery(id+"F8.imprint","IMPRINT",EDGE,{"derivedFrom":makeQuery(id+"F0.imprint","IMPRINT",EDGE,{"derivedFrom":sQuery(id+"F0.wireOp",EDGE,"E114.sketch_text.stroke-233")})}),-1.0]])]});
            var Q75;
            Q75=makeQuery(id+"F8.imprint","IMPRINT",FACE,{"disambiguationData":[TD([[makeQuery(id+"F8.imprint","IMPRINT",EDGE,{"derivedFrom":makeQuery(id+"F0.imprint","IMPRINT",EDGE,{"derivedFrom":sQuery(id+"F0.wireOp",EDGE,"E114.sketch_text.stroke-243")})}),-1.0]])]});
            var Q76;
            Q76=makeQuery(id+"F8.imprint","IMPRINT",FACE,{"disambiguationData":[TD([[makeQuery(id+"F8.imprint","IMPRINT",EDGE,{"derivedFrom":makeQuery(id+"F0.imprint","IMPRINT",EDGE,{"derivedFrom":sQuery(id+"F0.wireOp",EDGE,"E114.sketch_text.stroke-248")})}),-1.0]])]});
            var Q77;
            Q77=makeQuery(id+"F8.imprint","IMPRINT",FACE,{"disambiguationData":[TD([[makeQuery(id+"F8.imprint","IMPRINT",EDGE,{"derivedFrom":makeQuery(id+"F0.imprint","IMPRINT",EDGE,{"derivedFrom":sQuery(id+"F0.wireOp",EDGE,"E114.sketch_text.stroke-252")})}),-1.0]])]});
            var Q78;
            Q78=makeQuery(id+"F8.imprint","IMPRINT",FACE,{"disambiguationData":[TD([[makeQuery(id+"F8.imprint","IMPRINT",EDGE,{"derivedFrom":makeQuery(id+"F0.imprint","IMPRINT",EDGE,{"derivedFrom":sQuery(id+"F0.wireOp",EDGE,"E114.sketch_text.stroke-269")})}),-1.0]])]});
            var Q79;
            Q79=makeQuery(id+"F8.imprint","IMPRINT",FACE,{"disambiguationData":[TD([[makeQuery(id+"F8.imprint","IMPRINT",EDGE,{"derivedFrom":makeQuery(id+"F0.imprint","IMPRINT",EDGE,{"derivedFrom":sQuery(id+"F0.wireOp",EDGE,"E114.sketch_text.stroke-292")})}),-1.0]])]});
            var Q80;
            Q80=makeQuery(id+"F8.imprint","IMPRINT",FACE,{"disambiguationData":[TD([[makeQuery(id+"F8.imprint","IMPRINT",EDGE,{"derivedFrom":makeQuery(id+"F0.imprint","IMPRINT",EDGE,{"derivedFrom":sQuery(id+"F0.wireOp",EDGE,"E115.sketch_text.stroke-0")})}),-1.0]])]});
            var Q81;
            Q81=makeQuery(id+"F8.imprint","IMPRINT",FACE,{"disambiguationData":[TD([[makeQuery(id+"F8.imprint","IMPRINT",EDGE,{"derivedFrom":makeQuery(id+"F0.imprint","IMPRINT",EDGE,{"derivedFrom":sQuery(id+"F0.wireOp",EDGE,"E115.sketch_text.stroke-12")})}),-1.0]])]});
            var Q82;
            Q82=makeQuery(id+"F8.imprint","IMPRINT",FACE,{"disambiguationData":[TD([[makeQuery(id+"F8.imprint","IMPRINT",EDGE,{"derivedFrom":makeQuery(id+"F0.imprint","IMPRINT",EDGE,{"derivedFrom":sQuery(id+"F0.wireOp",EDGE,"E115.sketch_text.stroke-25")})}),-1.0]])]});
            var Q83;
            Q83=makeQuery(id+"F8.imprint","IMPRINT",FACE,{"disambiguationData":[TD([[makeQuery(id+"F8.imprint","IMPRINT",EDGE,{"derivedFrom":makeQuery(id+"F0.imprint","IMPRINT",EDGE,{"derivedFrom":sQuery(id+"F0.wireOp",EDGE,"E115.sketch_text.stroke-30")})}),-1.0]])]});
            var Q84;
            Q84=makeQuery(id+"F8.imprint","IMPRINT",FACE,{"disambiguationData":[TD([[makeQuery(id+"F8.imprint","IMPRINT",EDGE,{"derivedFrom":makeQuery(id+"F0.imprint","IMPRINT",EDGE,{"derivedFrom":sQuery(id+"F0.wireOp",EDGE,"E115.sketch_text.stroke-34")})}),-1.0]])]});
            var Q85;
            Q85=makeQuery(id+"F8.imprint","IMPRINT",FACE,{"disambiguationData":[TD([[makeQuery(id+"F8.imprint","IMPRINT",EDGE,{"derivedFrom":makeQuery(id+"F0.imprint","IMPRINT",EDGE,{"derivedFrom":sQuery(id+"F0.wireOp",EDGE,"E115.sketch_text.stroke-48")})}),-1.0]])]});
            var Q86;
            Q86=makeQuery(id+"F8.imprint","IMPRINT",FACE,{"disambiguationData":[TD([[makeQuery(id+"F8.imprint","IMPRINT",EDGE,{"derivedFrom":makeQuery(id+"F0.imprint","IMPRINT",EDGE,{"derivedFrom":sQuery(id+"F0.wireOp",EDGE,"E115.sketch_text.stroke-73")})}),-1.0]])]});
            var Q87;
            Q87=makeQuery(id+"F8.imprint","IMPRINT",FACE,{"disambiguationData":[TD([[makeQuery(id+"F8.imprint","IMPRINT",EDGE,{"derivedFrom":makeQuery(id+"F0.imprint","IMPRINT",EDGE,{"derivedFrom":sQuery(id+"F0.wireOp",EDGE,"E115.sketch_text.stroke-85")})}),-1.0]])]});
            var Q88;
            Q88=makeQuery(id+"F8.imprint","IMPRINT",FACE,{"disambiguationData":[TD([[makeQuery(id+"F8.imprint","IMPRINT",EDGE,{"derivedFrom":makeQuery(id+"F0.imprint","IMPRINT",EDGE,{"derivedFrom":sQuery(id+"F0.wireOp",EDGE,"E115.sketch_text.stroke-99")})}),-1.0]])]});
            var Q89;
            Q89=makeQuery(id+"F8.imprint","IMPRINT",FACE,{"disambiguationData":[TD([[makeQuery(id+"F8.imprint","IMPRINT",EDGE,{"derivedFrom":makeQuery(id+"F0.imprint","IMPRINT",EDGE,{"derivedFrom":sQuery(id+"F0.wireOp",EDGE,"E115.sketch_text.stroke-113")})}),-1.0]])]});
            var Q90;
            Q90=makeQuery(id+"F8.imprint","IMPRINT",FACE,{"disambiguationData":[TD([[makeQuery(id+"F8.imprint","IMPRINT",EDGE,{"derivedFrom":makeQuery(id+"F0.imprint","IMPRINT",EDGE,{"derivedFrom":sQuery(id+"F0.wireOp",EDGE,"E115.sketch_text.stroke-117")})}),-1.0]])]});
            var Q91;
            Q91=makeQuery(id+"F8.imprint","IMPRINT",FACE,{"disambiguationData":[TD([[makeQuery(id+"F8.imprint","IMPRINT",EDGE,{"derivedFrom":sQuery(id+"F8.wireOp",EDGE,"E117.bottom")}),-1.0]])]});
            var Q92;
            Q92=makeQuery(id+"F8.imprint","IMPRINT",FACE,{"disambiguationData":[TD([[makeQuery(id+"F8.imprint","IMPRINT",EDGE,{"derivedFrom":sQuery(id+"F8.wireOp",EDGE,"E120.bottom")}),-1.0]])]});
            var Q93;
            Q93=makeQuery(id+"F8.imprint","IMPRINT",FACE,{"disambiguationData":[TD([[makeQuery(id+"F8.imprint","IMPRINT",EDGE,{"derivedFrom":sQuery(id+"F8.wireOp",EDGE,"E118.bottom")}),-1.0]])]});
            var Q94;
            Q94=makeQuery(id+"F8.imprint","IMPRINT",FACE,{"disambiguationData":[TD([[makeQuery(id+"F8.imprint","IMPRINT",EDGE,{"derivedFrom":sQuery(id+"F8.wireOp",EDGE,"E119.bottom")}),1.0]])]});
            extrude(context, id + "F9", {"entities" : qUnion([Q0, Q1, Q2, Q3, Q4, Q5, Q6, Q7, Q8, Q9, Q10, Q11, Q12, Q13, Q14, Q15, Q16, Q17, Q18, Q19, Q20, Q21, Q22, Q23, Q24, Q25, Q26, Q27, Q28, Q29, Q30, Q31, Q32, Q33, Q34, Q35, Q36, Q37, Q38, Q39, Q40, Q41, Q42, Q43, Q44, Q45, Q46, Q47, Q48, Q49, Q50, Q51, Q52, Q53, Q54, Q55, Q56, Q57, Q58, Q59, Q60, Q61, Q62, Q63, Q64, Q65, Q66, Q67, Q68, Q69, Q70, Q71, Q72, Q73, Q74, Q75, Q76, Q77, Q78, Q79, Q80, Q81, Q82, Q83, Q84, Q85, Q86, Q87, Q88, Q89, Q90, Q91, Q92, Q93, Q94]), "depth" : 5 * mm, "offsetDistance" : 25 * mm});
        }
    });
